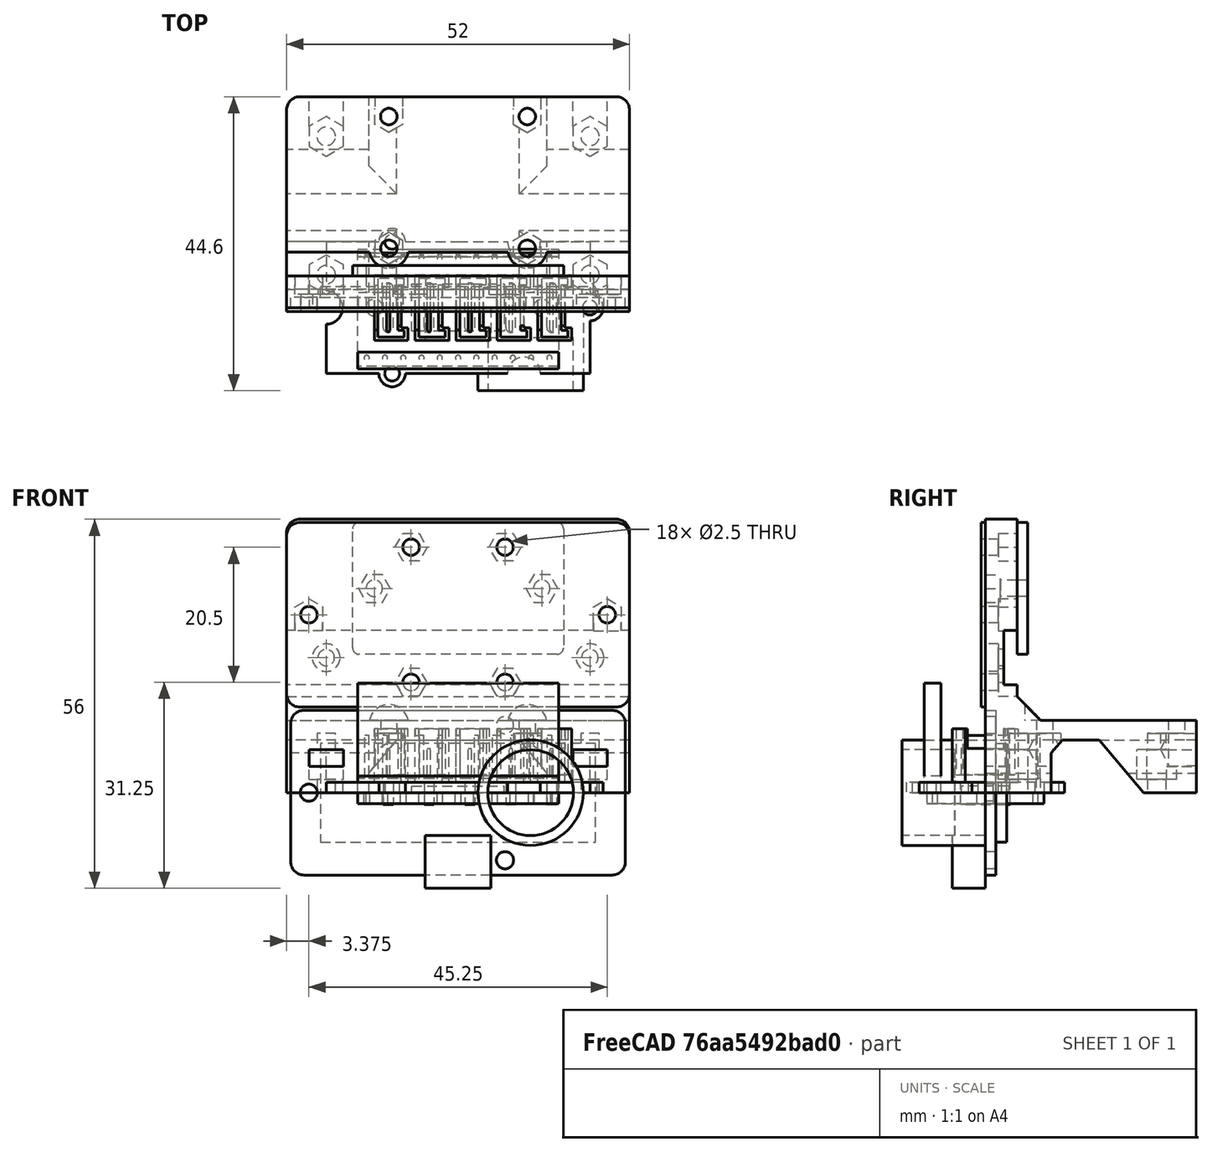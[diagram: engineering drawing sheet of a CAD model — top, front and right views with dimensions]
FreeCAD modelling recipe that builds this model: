
FCSTD DOCUMENT  (FreeCAD 0.19R24276 (Git))
Label: PB3D_TriPlate_USMount
License: All rights reserved
LicenseURL: http://en.wikipedia.org/wiki/All_rights_reserved
objects: Sketcher::SketchObject×54, PartDesign::Pocket×32, PartDesign::Body×30, PartDesign::Pad×20, PartDesign::FeatureBase×14, PartDesign::Plane×8, App::Part×5, PartDesign::LinearPattern×4, Spreadsheet::Sheet×3, Mesh::Feature×2, PartDesign::ShapeBinder×1, PartDesign::Fillet×1
note: 217 computed .brp shape members not serialized (recipe doc carries the construction recipe); baked Part::Feature solids carry a one-line shape summary decoded from their .brp

FEATURE [Spreadsheet::Sheet] Spreadsheet  label="params"
  cells = A1=M2 Bolt Clearances; C1=M2.5 Bolt Clearances; A2=Hole Clear Diam; B2(m2_hole_clear_diam)==2.5mm; C2=Hole Clear Diam; D2(m25_hole_clear_diam)==2.8mm; E2=Std Rad; F2(std_rad)==2mm; A3=Head Clear Diam; B3(m2_head_clear_diam)==4.2mm; C3=Head Clear Diam; D3(m25_head_clear_diam)==5.2mm; E3=Std Rad Min; F3(std_rad_min)==0.6mm; A4=Head Min Depth; B4(m2_head_min_depth)==2mm; C4=Head Min Depth; D4(m25_head_min_depth)==2.3mm; E4=Std Tol Clear; F4(std_tol_clear)==0.3mm; A5=Nut Clear Flat; B5(m2_nut_clear_flat)==4.2mm; C5=Nut Clear Flat; D5(m25_nut_clear_flat)==5.2mm; A6=Nut Min Depth; B6(m2_nut_min_depth)==2mm; C6=Nut Min Depth; D6(m25_nut_min_depth)==2mm; A8=USR Mount; C8=USR Mt To Plate; E8=Grove I2C Hub Mt; G8=Adafruit I2C Exp; A9=USR Mt Width; B9(usr_mt_width)==52mm; C9=MtToPlate Hole Space Offset W; D9(mt_to_plate_hole_space_offset_w)==6mm; E9=I2C Mt Plate Height; F9(i2c_mt_plate_height)==11mm; G9=Exp I2C Mt Height; H9(exp_i2c_mt_height)==31mm; A10=USR Mt Height; B10(usr_mt_height)==41.5mm; C10=MtToPlate Hole Space W; D10(mt_to_plate_hole_space_w)==usr_mt_width - 2 * mt_to_plate_hole_space_offset_w; E10=I2C Mt Plate Thick; F10(i2c_mt_plate_thick)==3mm; G10=Exp I2C Hole Space; H10(exp_i2c_hole_space)==25.4mm; A11=USR Mt Vert Thick; B11(usr_mt_vert_thick_top)==4.8mm; C11=MtToPlate Hole Offset L; D11(mt_to_plate_hole_offset_l)==5mm; E11=I2C Mt Nut Offset; F11(i2c_mt_nut_offset)==2mm; A12=USR Mt Vert Thick Bot; B12(usr_mt_vert_thick_bot)==8.4mm; C12=MtToPlate Hole Loc L; D12(mt_to_plate_hole_loc_l)==26mm; E12=I2C Mt Slot Z; F12(i2c_mt_slot_z)==i2c_mt_plate_height - i2c_mt_nut_offset; A13=USR Mt Foot Width; B13(usr_mt_foot_width)==32mm; E13=I2C Mt Slot Height; F13(i2c_mt_slot_height)==m2_nut_min_depth + 0.5mm; C14=MtToPlate CSunk Z; D14(mt_to_plate_csunk_z)==2mm; E14=I2C Mt CSunk Z; F14(i2c_mt_csunk_z)==i2c_mt_plate_height - i2c_mt_nut_offset; G14=LightSens Mts; A15=USR Mt Hole Width Long; B15(usr_mt_hole_width_long)==22.625mm; C15=MtToPlate CSunk Height; D15(mt_to_plate_csunk_height)==2mm; E15=I2C Mt CSunk Height; F15(i2c_mt_csunk_height)==m2_nut_min_depth; G15=LightSens Loc Z; H15(lightsens_loc_z)==16.5mm; A16=USR Mt Hole Width Short; B16(usr_mt_hole_width_short)==7.125mm; C16=MtToPlate Slot Z; D16(mt_to_plate_slot_z)==mt_to_plate_csunk_z + mt_to_plate_csunk_height; G16=LightMt Height; H16(lightmt_height)==8mm; A17=USR Mt Hole Height; B17(usr_mt_hole_height)==20.5mm; C17=MtToPlate Slot Height; D17(mt_to_plate_slot_height)==m25_nut_min_depth + 0.5mm; E17=I2C Mt Holes Width; F17(i2c_mt_holes_width)==21mm; G17=LightMt Hole Space Leng; H17(lightmt_hole_space_leng)==40mm; A18=USR Mt Hole Cent Loc Z; B18(usr_mt_hole_cent_loc_z)==27mm; E18=I2C Mt Holes Length; F18(i2c_mt_holes_length)==20mm; G18=LightMt Cent Thick; H18(lightmt_thick_cent)==2mm; E19=I2C Mt Holes Offset Leng; F19(i2c_mt_holes_offset_leng)==9mm; A20=USR CSunk Offset; B20(usr_mt_csunk_offset)==2mm; E21=I2C Plate Clear Diam; F21(i2c_plate_clear_diam)==6mm; A22=USR Mt Fr Arch Width; B22(usr_mt_fr_arch_width)==27mm; A23=USR Mt Fr Arch Vert Height; B23(usr_mt_fr_arch_vert_height)==3mm; A24=USR Mt Si Arch Width; B24(usr_mt_side_arch_width)==14mm; A25=USR Mt Si Arch Offset; B25(usr_mt_side_arch_offset)==8mm; A26=USR Mt Si Arch Vert Height; B26(usr_mt_side_arch_vert_height)==6mm
FEATURE [Sketcher::SketchObject] Sketch001
  FullyConstrained = true
  MapMode = 5
  Placement = pos=(0,0,0) rot=(1,0,0;1.5708rad)
  Support = -> [XZ_Plane006]
  sketch-geometry (5):
    g0: Circle CenterX=-22.625 CenterY=0 CenterZ=0 NormalX=0 NormalY=0 NormalZ=1 AngleXU=0 Radius=1.3
    g1: Circle CenterX=7.125 CenterY=10.25 CenterZ=0 NormalX=0 NormalY=0 NormalZ=1 AngleXU=0 Radius=1.3
    g2: Circle CenterX=7.125 CenterY=-10.25 CenterZ=0 NormalX=0 NormalY=0 NormalZ=1 AngleXU=0 Radius=1.3
    g3: LineSegment StartX=7.125 StartY=10.25 StartZ=0 EndX=7.125 EndY=-10.25 EndZ=0
    g4: LineSegment StartX=0 StartY=0 StartZ=0 EndX=7.125 EndY=0 EndZ=0
  constraints (13):
    c: PointOnObject(g0,g-1)
    c: Coincident(g3,g1)
    c: Coincident(g3,g2)
    c: Vertical(g3)
    c: Equal(g0,g1)
    c: Equal(g2,g1)
    c: Diameter(g0) = 2.6
    c: Coincident(g4,g-1)
    c: PointOnObject(g4,g-1)
    c: Symmetric(g1,g2,g4)
    c: Distance(g3) = 20.5
    c: Distance(g4) = 7.125
    c: DistanceX(g0,g-1) = 22.625
FEATURE [PartDesign::ShapeBinder] CopyPocket
  Placement = pos=(0,0,0) rot=(1,0,0;1.5708rad)
  TraceSupport = false
FEATURE [Sketcher::SketchObject] Sketch
  FullyConstrained = true
  MapMode = 5
  Placement = pos=(0,0,0) rot=(1,0,0;1.5708rad)
  Support = -> [XZ_Plane006]
  sketch-geometry (6):
    g0: LineSegment StartX=0 StartY=0 StartZ=0 EndX=0 EndY=12.5 EndZ=0
    g1: LineSegment StartX=0 StartY=0 StartZ=0 EndX=25.375 EndY=0 EndZ=0
    g2: LineSegment StartX=-25.375 StartY=12.5 StartZ=0 EndX=25.375 EndY=12.5 EndZ=0
    g3: LineSegment StartX=25.375 StartY=12.5 StartZ=0 EndX=25.375 EndY=-12.5 EndZ=0
    g4: LineSegment StartX=25.375 StartY=-12.5 StartZ=0 EndX=-25.375 EndY=-12.5 EndZ=0
    g5: LineSegment StartX=-25.375 StartY=-12.5 StartZ=0 EndX=-25.375 EndY=12.5 EndZ=0
  constraints (16):
    c: Coincident(g0,g-1)
    c: PointOnObject(g0,g-2)
    c: Coincident(g1,g-1)
    c: Horizontal(g1)
    c: Coincident(g2,g3)
    c: Coincident(g3,g4)
    c: Coincident(g4,g5)
    c: Coincident(g5,g2)
    c: Horizontal(g2)
    c: Horizontal(g4)
    c: Vertical(g3)
    c: Vertical(g5)
    c: Symmetric(g2,g2,g0)
    c: Symmetric(g2,g3,g1)
    c: Distance(g2) = 50.75
    c: Distance(g3) = 25
FEATURE [PartDesign::Pad] Pad
  Direction = (1,1,1)
  Length = 1.6
  Length2 = 100
  Placement = pos=(0,0,0) rot=(1,0,0;1.5708rad)
  Profile = -> Sketch
  Reversed = true
  Type = 0
FEATURE [PartDesign::Fillet] Fillet
  Base = -> Pad [Edge2,Edge1,Edge8,Edge5]
  BaseFeature = -> Pad
  Placement = pos=(0,0,0) rot=(1,0,0;1.5708rad)
  Radius = 2
  SupportTransform = false
FEATURE [PartDesign::Pocket] Pocket
  BaseFeature = -> Fillet
  Length = 5
  Length2 = 100
  Placement = pos=(0,0,0) rot=(1,0,0;1.5708rad)
  Profile = -> Sketch001
  Type = 1
FEATURE [PartDesign::Body] Body005  label="MainPlate"
  Group = -> [Sketch,Pad,Fillet,Sketch001,Pocket]
  Origin = -> Origin007
  Tip = -> Pocket
FEATURE [Sketcher::SketchObject] Sketch002
  FullyConstrained = true
  MapMode = 5
  Placement = pos=(0,0,0) rot=(1,0,0;1.5708rad)
  Support = -> [XZ_Plane002]
  sketch-geometry (1):
    g0: Circle CenterX=-11 CenterY=0 CenterZ=0 NormalX=0 NormalY=0 NormalZ=1 AngleXU=0 Radius=8
  constraints (3):
    c: PointOnObject(g0,g-1)
    c: DistanceX(g0,g-1) = 11
    c: Diameter(g0) = 16
FEATURE [PartDesign::Pad] Pad001
  Direction = (1,1,1)
  Length = 12.6
  Length2 = 100
  Placement = pos=(0,0,0) rot=(1,0,0;1.5708rad)
  Profile = -> Sketch002
  Type = 0
FEATURE [Sketcher::SketchObject] Sketch004
  FullyConstrained = true
  MapMode = 5
  Placement = pos=(0,0,0) rot=(1,0,0;1.5708rad)
  Support = -> [XZ_Plane004]
  sketch-geometry (5):
    g0: LineSegment StartX=-5 StartY=-6.5 StartZ=0 EndX=5 EndY=-6.5 EndZ=0
    g1: LineSegment StartX=5 StartY=-6.5 StartZ=0 EndX=5 EndY=-14.5 EndZ=0
    g2: LineSegment StartX=5 StartY=-14.5 StartZ=0 EndX=-5 EndY=-14.5 EndZ=0
    g3: LineSegment StartX=-5 StartY=-14.5 StartZ=0 EndX=-5 EndY=-6.5 EndZ=0
    g4: LineSegment StartX=0 StartY=0 StartZ=0 EndX=0 EndY=-6.5 EndZ=0
  constraints (14):
    c: Coincident(g0,g1)
    c: Coincident(g1,g2)
    c: Coincident(g2,g3)
    c: Coincident(g3,g0)
    c: Horizontal(g0)
    c: Horizontal(g2)
    c: Vertical(g1)
    c: Vertical(g3)
    c: Coincident(g4,g-1)
    c: Vertical(g4)
    c: Symmetric(g0,g0,g4)
    c: Distance(g4) = 6.5
    c: Distance(g1) = 8
    c: Distance(g2) = 10
FEATURE [PartDesign::Pad] Pad002
  Direction = (1,1,1)
  Length = 5
  Length2 = 100
  Placement = pos=(0,0,0) rot=(1,0,0;1.5708rad)
  Profile = -> Sketch004
  Type = 0
FEATURE [PartDesign::Body] Body003  label="GroveConnector"
  Group = -> [Sketch004,Pad002]
  Origin = -> Origin004
  Tip = -> Pad002
FEATURE [Sketcher::SketchObject] Sketch003
  FullyConstrained = true
  MapMode = 5
  Placement = pos=(0,-12.6,5.6e-15) rot=(1,0,0;1.5708rad)
  Support = -> [Pad001]
  sketch-geometry (1):
    g0: Circle CenterX=-11 CenterY=0 CenterZ=0 NormalX=0 NormalY=0 NormalZ=1 AngleXU=0 Radius=6.5
  constraints (3):
    c: PointOnObject(g0,g-1)
    c: DistanceX(g0,g-1) = 11
    c: Diameter(g0) = 13
FEATURE [PartDesign::Pocket] Pocket001
  BaseFeature = -> Pad001
  Length = 8
  Length2 = 100
  Placement = pos=(0,0,0) rot=(1,0,0;1.5708rad)
  Profile = -> Sketch003
  Type = 0
FEATURE [PartDesign::Body] Body001  label="USProbeL"
  Group = -> [Sketch002,Pad001,Sketch003,Pocket001]
  Origin = -> Origin006
  Tip = -> Pocket001
FEATURE [Sketcher::SketchObject] Sketch005
  FullyConstrained = true
  MapMode = 5
  Placement = pos=(0,1.6,-7e-16) rot=(-1,0,0;1.5708rad)
  Support = -> [CopyPocket]
  sketch-geometry (6):
    g0: LineSegment StartX=0 StartY=0 StartZ=0 EndX=0 EndY=7.5 EndZ=0
    g1: LineSegment StartX=0 StartY=0 StartZ=0 EndX=20.875 EndY=0 EndZ=0
    g2: LineSegment StartX=-20.875 StartY=7.5 StartZ=0 EndX=20.875 EndY=7.5 EndZ=0
    g3: LineSegment StartX=20.875 StartY=7.5 StartZ=0 EndX=20.875 EndY=-7.5 EndZ=0
    g4: LineSegment StartX=20.875 StartY=-7.5 StartZ=0 EndX=-20.875 EndY=-7.5 EndZ=0
    g5: LineSegment StartX=-20.875 StartY=-7.5 StartZ=0 EndX=-20.875 EndY=7.5 EndZ=0
  constraints (16):
    c: Coincident(g0,g-1)
    c: Vertical(g0)
    c: Coincident(g1,g-1)
    c: Horizontal(g1)
    c: Coincident(g2,g3)
    c: Coincident(g3,g4)
    c: Coincident(g4,g5)
    c: Coincident(g5,g2)
    c: Horizontal(g2)
    c: Horizontal(g4)
    c: Vertical(g3)
    c: Vertical(g5)
    c: Symmetric(g2,g2,g0)
    c: Symmetric(g2,g3,g1)
    c: Distance(g3) = 15
    c: Distance(g2) = 41.75
FEATURE [PartDesign::Pad] Pad003
  Direction = (1,1,1)
  Length = 1.65
  Length2 = 100
  Placement = pos=(0,0,0) rot=(1,0,0;1.5708rad)
  Profile = -> Sketch005
  Type = 0
FEATURE [PartDesign::Body] Body004  label="Chips"
  Group = -> [CopyPocket,Sketch005,Pad003]
  Origin = -> Origin005
  Tip = -> Pad003
FEATURE [PartDesign::FeatureBase] Clone
  BaseFeature = -> Body001
FEATURE [PartDesign::Body] Body002  label="USProbeR"
  BaseFeature = -> Body001
  Group = -> [Clone]
  Origin = -> Origin003
  Placement = pos=(22,0,0) rot=(0,0,1;0rad)
  Tip = -> Clone
FEATURE [App::Part] Part001  label="Grove_USRanger"
  Group = -> [Body005,Body001,Body002,Body003,Body004]
  Origin = -> Origin002
  Placement = pos=(0,-4,27) rot=(0,0,1;0rad)
FEATURE [Sketcher::SketchObject] Sketch012
  FullyConstrained = true
  MapMode = 5
  Support = -> [XY_Plane014]
  sketch-geometry (6):
    g0: Circle CenterX=-10 CenterY=10 CenterZ=0 NormalX=0 NormalY=0 NormalZ=1 AngleXU=0 Radius=1.125
    g1: Circle CenterX=-10 CenterY=-10 CenterZ=0 NormalX=0 NormalY=0 NormalZ=1 AngleXU=0 Radius=1.125
    g2: Circle CenterX=20 CenterY=0 CenterZ=0 NormalX=0 NormalY=0 NormalZ=1 AngleXU=0 Radius=1.125
    g3: LineSegment StartX=-10 StartY=10 StartZ=0 EndX=-10 EndY=-10 EndZ=0
    g4: LineSegment StartX=0 StartY=0 StartZ=0 EndX=20 EndY=0 EndZ=0
    g5: LineSegment StartX=0 StartY=0 StartZ=0 EndX=-10 EndY=0 EndZ=0
  constraints (15):
    c: Coincident(g3,g0)
    c: Coincident(g3,g1)
    c: Coincident(g4,g-1)
    c: Coincident(g4,g2)
    c: Horizontal(g4)
    c: Coincident(g5,g-1)
    c: PointOnObject(g5,g-1)
    c: Symmetric(g0,g1,g5)
    c: Vertical(g3)
    c: Equal(g2,g0)
    c: Equal(g0,g1)
    c: Diameter(g0) = 2.25
    c: Distance(g5) = 10
    c: Distance(g4) = 20
    c: Distance(g3) = 20
FEATURE [Sketcher::SketchObject] Sketch013
  FullyConstrained = true
  MapMode = 5
  Support = -> [XY_Plane014]
  sketch-geometry (26):
    g0: LineSegment StartX=-20 StartY=10 StartZ=0 EndX=-12 EndY=10 EndZ=0
    g1: LineSegment StartX=-8 StartY=10 StartZ=0 EndX=0 EndY=10 EndZ=0
    g2: LineSegment StartX=0 StartY=10 StartZ=0 EndX=7.5 EndY=10 EndZ=0
    g3: LineSegment StartX=12.5 StartY=10 StartZ=0 EndX=20 EndY=10 EndZ=0
    g4: LineSegment StartX=20 StartY=-10 StartZ=0 EndX=12.5 EndY=-10 EndZ=0
    g5: LineSegment StartX=7.5 StartY=-10 StartZ=0 EndX=0 EndY=-10 EndZ=0
    g6: LineSegment StartX=0 StartY=-10 StartZ=0 EndX=-8 EndY=-10 EndZ=0
    g7: LineSegment StartX=-12 StartY=-10 StartZ=0 EndX=-20 EndY=-10 EndZ=0
    g8: LineSegment StartX=-12 StartY=10 StartZ=0 EndX=-8 EndY=10 EndZ=0
    g9: LineSegment StartX=-12 StartY=-10 StartZ=0 EndX=-8 EndY=-10 EndZ=0
    g10: LineSegment StartX=7.5 StartY=10 StartZ=0 EndX=12.5 EndY=10 EndZ=0
    g11: LineSegment StartX=7.5 StartY=-10 StartZ=0 EndX=12.5 EndY=-10 EndZ=0
    g12: LineSegment StartX=20 StartY=10 StartZ=0 EndX=20 EndY=2 EndZ=0
    g13: LineSegment StartX=20 StartY=-10 StartZ=0 EndX=20 EndY=-2 EndZ=0
    g14: LineSegment StartX=-20 StartY=-2.5 StartZ=0 EndX=-20 EndY=2.5 EndZ=0
    g15: LineSegment StartX=20 StartY=2 StartZ=0 EndX=20 EndY=-2 EndZ=0
    g16: ArcOfCircle CenterX=20 CenterY=0 CenterZ=0 NormalX=0 NormalY=0 NormalZ=1 AngleXU=0 Radius=2 StartAngle=4.71239 EndAngle=7.85398
    g17: ArcOfCircle CenterX=-10 CenterY=10 CenterZ=0 NormalX=0 NormalY=0 NormalZ=1 AngleXU=0 Radius=2 StartAngle=-9e-16 EndAngle=3.14159
    g18: ArcOfCircle CenterX=-10 CenterY=-10 CenterZ=0 NormalX=0 NormalY=0 NormalZ=1 AngleXU=0 Radius=2 StartAngle=3.14159 EndAngle=6.28319
    g19: ArcOfCircle CenterX=10 CenterY=10 CenterZ=0 NormalX=0 NormalY=0 NormalZ=1 AngleXU=0 Radius=2.5 StartAngle=3.14159 EndAngle=6.28319
    g20: ArcOfCircle CenterX=10 CenterY=-10 CenterZ=0 NormalX=0 NormalY=0 NormalZ=1 AngleXU=0 Radius=2.5 StartAngle=1e-15 EndAngle=3.14159
    g21: LineSegment StartX=-10 StartY=10 StartZ=0 EndX=-10 EndY=-10 EndZ=0
    g22: LineSegment StartX=10 StartY=10 StartZ=0 EndX=10 EndY=-10 EndZ=0
    g23: LineSegment StartX=-20 StartY=10 StartZ=0 EndX=-20 EndY=2.5 EndZ=0
    g24: LineSegment StartX=-20 StartY=-10 StartZ=0 EndX=-20 EndY=-2.5 EndZ=0
    g25: ArcOfCircle CenterX=-20 CenterY=0 CenterZ=0 NormalX=0 NormalY=0 NormalZ=1 AngleXU=0 Radius=2.5 StartAngle=4.71239 EndAngle=7.85398
  constraints (76):
    c: Horizontal(g0)
    c: PointOnObject(g1,g-2)
    c: Horizontal(g1)
    c: Coincident(g2,g1)
    c: Horizontal(g2)
    c: Horizontal(g3)
    c: Horizontal(g4)
    c: PointOnObject(g5,g-2)
    c: Horizontal(g5)
    c: Coincident(g6,g5)
    c: Horizontal(g6)
    c: Horizontal(g7)
    c: Coincident(g8,g0)
    c: Coincident(g8,g1)
    c: Horizontal(g8)
    c: Coincident(g9,g7)
    c: Coincident(g9,g6)
    c: Coincident(g10,g2)
    c: Coincident(g10,g3)
    c: Horizontal(g10)
    c: Coincident(g11,g5)
    c: Coincident(g11,g4)
    c: Horizontal(g11)
    c: Horizontal(g9)
    c: Coincident(g12,g3)
    c: Coincident(g13,g4)
    c: Vertical(g13)
    c: Vertical(g14)
    c: Coincident(g15,g12)
    c: Coincident(g15,g13)
    c: Vertical(g15)
    c: Vertical(g12)
    c: PointOnObject(g16,g-1)
    c: Coincident(g16,g12)
    c: Coincident(g16,g13)
    c: PointOnObject(g16,g15)
    c: Coincident(g17,g0)
    c: Coincident(g17,g1)
    c: Coincident(g18,g7)
    c: Coincident(g18,g6)
    c: Coincident(g19,g2)
    c: Coincident(g19,g3)
    c: Coincident(g20,g5)
    c: Coincident(g20,g4)
    c: Coincident(g21,g17)
    c: Coincident(g21,g18)
    c: Vertical(g21)
    c: Coincident(g22,g19)
    c: Coincident(g22,g20)
    c: Vertical(g22)
    c: Equal(g17,g18)
    c: Equal(g18,g16)
    c: Equal(g20,g19)
    c: PointOnObject(g19,g10)
    c: PointOnObject(g20,g11)
    c: PointOnObject(g17,g8)
    c: PointOnObject(g18,g9)
    c: Diameter(g17) = 4
    c: Equal(g1,g0)
    c: Equal(g2,g3)
    c: DistanceX(g0,g3) = 40
    c: DistanceX(g1,g3) = 20
    c: DistanceY(g4,g3) = 20
    c: Coincident(g23,g0)
    c: Vertical(g23)
    c: Coincident(g24,g7)
    c: Vertical(g24)
    c: Equal(g23,g24)
    c: PointOnObject(g25,g-1)
    c: Coincident(g25,g23)
    c: Coincident(g25,g24)
    c: Diameter(g19) = 5
    c: Equal(g25,g19)
    c: PointOnObject(g25,g14)
    c: Coincident(g14,g23)
    c: Coincident(g14,g24)
FEATURE [PartDesign::Pad] Pad008
  Direction = (1,1,1)
  Length = 1.6
  Length2 = 100
  Profile = -> Sketch013
  Type = 0
FEATURE [PartDesign::Pocket] Pocket004
  BaseFeature = -> Pad008
  Length = 5
  Length2 = 100
  Profile = -> Sketch012
  Reversed = true
  Type = 1
FEATURE [PartDesign::Body] Body006  label="GroveDBoard"
  Group = -> [Sketch013,Pad008,Sketch012,Pocket004]
  Origin = -> Origin008
  Tip = -> Pocket004
FEATURE [Sketcher::SketchObject] Sketch008
  FullyConstrained = true
  MapMode = 5
  Support = -> [XY_Plane015]
  sketch-geometry (8):
    g0: LineSegment StartX=-5 StartY=0 StartZ=0 EndX=-3.05 EndY=0 EndZ=0
    g1: LineSegment StartX=3.05 StartY=0 StartZ=0 EndX=5 EndY=0 EndZ=0
    g2: LineSegment StartX=-5 StartY=0 StartZ=0 EndX=-5 EndY=5.1 EndZ=0
    g3: LineSegment StartX=-5 StartY=5.1 StartZ=0 EndX=5 EndY=5.1 EndZ=0
    g4: LineSegment StartX=5 StartY=5.1 StartZ=0 EndX=5 EndY=0 EndZ=0
    g5: LineSegment StartX=3.05 StartY=0 StartZ=0 EndX=3.05 EndY=1 EndZ=0
    g6: LineSegment StartX=3.05 StartY=1 StartZ=0 EndX=-3.05 EndY=1 EndZ=0
    g7: LineSegment StartX=-3.05 StartY=1 StartZ=0 EndX=-3.05 EndY=0 EndZ=0
  constraints (23):
    c: PointOnObject(g0,g-1)
    c: PointOnObject(g1,g-1)
    c: PointOnObject(g0,g-1)
    c: Coincident(g2,g0)
    c: Vertical(g2)
    c: Coincident(g3,g2)
    c: Horizontal(g3)
    c: Coincident(g4,g3)
    c: Coincident(g4,g1)
    c: Vertical(g4)
    c: Coincident(g5,g1)
    c: Vertical(g5)
    c: Coincident(g6,g5)
    c: Horizontal(g6)
    c: Coincident(g7,g6)
    c: Coincident(g7,g0)
    c: Vertical(g7)
    c: Equal(g0,g1)
    c: Symmetric(g0,g1,g-1)
    c: Distance(g4) = 5.1
    c: Distance(g6) = 6.1
    c: Distance(g3) = 10
    c: Distance(g7) = 1
FEATURE [PartDesign::Pad] Pad005
  Direction = (1,1,1)
  Length = 8.1
  Length2 = 100
  Profile = -> Sketch008
  Type = 0
FEATURE [Sketcher::SketchObject] Sketch009
  FullyConstrained = true
  MapMode = 5
  Placement = pos=(0,0,8.1) rot=(0,0,1;0rad)
  Support = -> [Pad005]
  sketch-geometry (10):
    g0: LineSegment StartX=-4.45 StartY=0.55 StartZ=0 EndX=-3.45 EndY=0.55 EndZ=0
    g1: LineSegment StartX=-3.45 StartY=0.55 StartZ=0 EndX=-3.45 EndY=1.55 EndZ=0
    g2: LineSegment StartX=-3.45 StartY=1.55 StartZ=0 EndX=3.45 EndY=1.55 EndZ=0
    g3: LineSegment StartX=3.45 StartY=1.55 StartZ=0 EndX=3.45 EndY=0.55 EndZ=0
    g4: LineSegment StartX=3.45 StartY=0.55 StartZ=0 EndX=4.45 EndY=0.55 EndZ=0
    g5: LineSegment StartX=4.45 StartY=0.55 StartZ=0 EndX=4.45 EndY=4.55 EndZ=0
    g6: LineSegment StartX=4.45 StartY=4.55 StartZ=0 EndX=-4.45 EndY=4.55 EndZ=0
    g7: LineSegment StartX=-4.45 StartY=4.55 StartZ=0 EndX=-4.45 EndY=0.55 EndZ=0
    g8: LineSegment StartX=-3.45 StartY=0.55 StartZ=0 EndX=3.45 EndY=0.55 EndZ=0
    g9: LineSegment StartX=0 StartY=0 StartZ=0 EndX=0 EndY=0.55 EndZ=0
  constraints (28):
    c: Horizontal(g0)
    c: Coincident(g1,g0)
    c: Coincident(g2,g1)
    c: Horizontal(g2)
    c: Coincident(g3,g2)
    c: Vertical(g3)
    c: Coincident(g4,g3)
    c: Horizontal(g4)
    c: Coincident(g5,g4)
    c: Vertical(g5)
    c: Coincident(g6,g5)
    c: Horizontal(g6)
    c: Coincident(g7,g6)
    c: Coincident(g7,g0)
    c: Vertical(g7)
    c: Vertical(g1)
    c: Coincident(g8,g0)
    c: Coincident(g8,g3)
    c: Horizontal(g8)
    c: Equal(g0,g4)
    c: Coincident(g9,g-1)
    c: PointOnObject(g9,g-2)
    c: Symmetric(g0,g3,g9)
    c: Distance(g0) = 1
    c: Distance(g1) = 1
    c: Distance(g9) = 0.55
    c: Distance(g6) = 8.9
    c: DistanceY(g2,g5) = 3
FEATURE [PartDesign::Pocket] Pocket003
  BaseFeature = -> Pad005
  Length = 7
  Length2 = 100
  Profile = -> Sketch009
  Type = 0
FEATURE [Sketcher::SketchObject] Sketch014
  FullyConstrained = true
  MapMode = 5
  Support = -> [XY_Plane015]
  sketch-geometry (5):
    g0: ArcOfCircle CenterX=-3 CenterY=3 CenterZ=0 NormalX=0 NormalY=0 NormalZ=1 AngleXU=0 Radius=0.75 StartAngle=1.5708 EndAngle=4.71239
    g1: ArcOfCircle CenterX=3 CenterY=3 CenterZ=0 NormalX=0 NormalY=0 NormalZ=1 AngleXU=0 Radius=0.75 StartAngle=4.71239 EndAngle=7.85398
    g2: LineSegment StartX=-3 StartY=2.25 StartZ=0 EndX=3 EndY=2.25 EndZ=0
    g3: LineSegment StartX=-3 StartY=3.75 StartZ=0 EndX=3 EndY=3.75 EndZ=0
    g4: LineSegment StartX=0 StartY=0 StartZ=0 EndX=0 EndY=3 EndZ=0
  constraints (12):
    c: Tangent(g0,g3) = 1.5708
    c: Tangent(g0,g2) = -1.5708
    c: Tangent(g2,g1) = -1.5708
    c: Tangent(g3,g1) = 1.5708
    c: Horizontal(g2)
    c: Equal(g0,g1)
    c: Coincident(g4,g-1)
    c: PointOnObject(g4,g-2)
    c: Symmetric(g0,g1,g4)
    c: Distance(g4) = 3
    c: DistanceY(g1,g1) = 1.5
    c: DistanceX(g0,g1) = 6
FEATURE [Sketcher::SketchObject] Sketch010
  FullyConstrained = true
  MapMode = 5
  Placement = pos=(0,0,8.1) rot=(0,0,1;0rad)
  Support = -> [Pocket003]
  sketch-geometry (5):
    g0: LineSegment StartX=0 StartY=0 StartZ=0 EndX=0 EndY=3 EndZ=0
    g1: LineSegment StartX=-3.4 StartY=8 StartZ=0 EndX=3.4 EndY=8 EndZ=0
    g2: LineSegment StartX=3.4 StartY=8 StartZ=0 EndX=3.4 EndY=3 EndZ=0
    g3: LineSegment StartX=3.4 StartY=3 StartZ=0 EndX=-3.4 EndY=3 EndZ=0
    g4: LineSegment StartX=-3.4 StartY=3 StartZ=0 EndX=-3.4 EndY=8 EndZ=0
  constraints (14):
    c: Coincident(g0,g-1)
    c: PointOnObject(g0,g-2)
    c: Coincident(g1,g2)
    c: Coincident(g2,g3)
    c: Coincident(g3,g4)
    c: Coincident(g4,g1)
    c: Horizontal(g1)
    c: Horizontal(g3)
    c: Vertical(g2)
    c: Vertical(g4)
    c: Symmetric(g3,g2,g0)
    c: Distance(g0) = 3
    c: Distance(g2) = 5
    c: Distance(g1) = 6.8
FEATURE [PartDesign::Pocket] Pocket006
  BaseFeature = -> Pocket003
  Length = 1
  Length2 = 100
  Profile = -> Sketch010
  Type = 0
FEATURE [Sketcher::SketchObject] Sketch011
  FullyConstrained = true
  MapMode = 5
  Placement = pos=(0,0,8.1) rot=(0,0,1;0rad)
  Support = -> [Pocket006]
  sketch-geometry (4):
    g0: LineSegment StartX=-2.75 StartY=3 StartZ=0 EndX=2.75 EndY=3 EndZ=0
    g1: LineSegment StartX=2.75 StartY=3 StartZ=0 EndX=2.75 EndY=0 EndZ=0
    g2: LineSegment StartX=2.75 StartY=0 StartZ=0 EndX=-2.75 EndY=0 EndZ=0
    g3: LineSegment StartX=-2.75 StartY=0 StartZ=0 EndX=-2.75 EndY=3 EndZ=0
  constraints (11):
    c: Coincident(g0,g1)
    c: Coincident(g1,g2)
    c: Coincident(g2,g3)
    c: Coincident(g3,g0)
    c: Horizontal(g0)
    c: Horizontal(g2)
    c: Vertical(g1)
    c: Vertical(g3)
    c: Symmetric(g2,g1,g-1)
    c: Distance(g1) = 3
    c: Distance(g0) = 5.5
FEATURE [PartDesign::Pocket] Pocket005
  BaseFeature = -> Pocket006
  Length = 3
  Length2 = 100
  Profile = -> Sketch011
  Type = 0
FEATURE [Sketcher::SketchObject] Sketch015
  FullyConstrained = true
  MapMode = 5
  Placement = pos=(0,0,1.1) rot=(0,0,1;0rad)
  Support = -> [Pocket005]
  sketch-geometry (5):
    g0: ArcOfCircle CenterX=-3.4 CenterY=3 CenterZ=0 NormalX=0 NormalY=0 NormalZ=1 AngleXU=0 Radius=0.25 StartAngle=1.5708 EndAngle=4.71239
    g1: ArcOfCircle CenterX=3.4 CenterY=3 CenterZ=0 NormalX=0 NormalY=0 NormalZ=1 AngleXU=0 Radius=0.25 StartAngle=4.71239 EndAngle=7.85398
    g2: LineSegment StartX=-3.4 StartY=2.75 StartZ=0 EndX=3.4 EndY=2.75 EndZ=0
    g3: LineSegment StartX=-3.4 StartY=3.25 StartZ=0 EndX=3.4 EndY=3.25 EndZ=0
    g4: LineSegment StartX=0 StartY=0 StartZ=0 EndX=0 EndY=2.75 EndZ=0
  constraints (12):
    c: Tangent(g0,g3) = 1.5708
    c: Tangent(g0,g2) = -1.5708
    c: Tangent(g2,g1) = -1.5708
    c: Tangent(g3,g1) = 1.5708
    c: Horizontal(g2)
    c: Equal(g0,g1)
    c: Coincident(g4,g-1)
    c: PointOnObject(g4,g-2)
    c: Symmetric(g0,g1,g4)
    c: DistanceY(g-1,g1) = 3
    c: DistanceY(g1,g1) = 0.5
    c: DistanceX(g0,g1) = 6.8
FEATURE [PartDesign::Pad] Pad006
  BaseFeature = -> Pocket005
  Direction = (1,1,1)
  Length = 4
  Length2 = 100
  Profile = -> Sketch015
  Type = 0
FEATURE [PartDesign::Pad] Pad007
  BaseFeature = -> Pad006
  Direction = (1,1,1)
  Length = 3.4
  Length2 = 100
  Profile = -> Sketch014
  Reversed = true
  Type = 0
FEATURE [PartDesign::Body] Body007  label="GroveHeader1"
  Group = -> [Sketch008,Pad005,Sketch009,Pocket003,Sketch010,Pocket006,Sketch011,Pocket005,Sketch015,Pad006,Sketch014,Pad007]
  Origin = -> Origin015
  Placement = pos=(-13.8,0,1.6) rot=(0,0,1;1.5708rad)
  Tip = -> Pad007
FEATURE [PartDesign::FeatureBase] Clone003
  BaseFeature = -> Body007
  Placement = pos=(-14,0,1.6) rot=(0,0,1;1.5708rad)
FEATURE [PartDesign::Body] Body009  label="GroveHeader5"
  BaseFeature = -> Body007
  Group = -> [Clone003]
  Origin = -> Origin013
  Placement = pos=(25,0,0) rot=(0,0,1;0rad)
  Tip = -> Clone003
FEATURE [PartDesign::FeatureBase] Clone002
  BaseFeature = -> Body007
  Placement = pos=(-14,0,1.6) rot=(0,0,1;1.5708rad)
FEATURE [PartDesign::Body] Body010  label="GroveHeader4"
  BaseFeature = -> Body007
  Group = -> [Clone002]
  Origin = -> Origin011
  Placement = pos=(18.8,0,0) rot=(0,0,1;0rad)
  Tip = -> Clone002
FEATURE [PartDesign::FeatureBase] Clone001
  BaseFeature = -> Body007
  Placement = pos=(-14,0,1.6) rot=(0,0,1;1.5708rad)
FEATURE [PartDesign::Body] Body008  label="GroveHeader3"
  BaseFeature = -> Body007
  Group = -> [Clone001]
  Origin = -> Origin010
  Placement = pos=(12.6,0,0) rot=(0,0,1;0rad)
  Tip = -> Clone001
FEATURE [PartDesign::FeatureBase] Clone004
  BaseFeature = -> Body007
  Placement = pos=(-14,0,1.6) rot=(0,0,1;1.5708rad)
FEATURE [PartDesign::Body] Body011  label="GroveHeader6"
  BaseFeature = -> Body007
  Group = -> [Clone004]
  Origin = -> Origin014
  Placement = pos=(31.2,0,0) rot=(0,0,1;0rad)
  Tip = -> Clone004
FEATURE [PartDesign::FeatureBase] Clone005
  BaseFeature = -> Body007
  Placement = pos=(-14,0,1.6) rot=(0,0,1;1.5708rad)
FEATURE [PartDesign::Body] Body012  label="GroveHeader2"
  BaseFeature = -> Body007
  Group = -> [Clone005]
  Origin = -> Origin012
  Placement = pos=(6.4,0,0) rot=(0,0,1;0rad)
  Tip = -> Clone005
FEATURE [App::Part] Part002  label="Grove_I2CHub6_Part1"
  Group = -> [Body006,Body007,Body012,Body008,Body010,Body009,Body011]
  Origin = -> Origin009
  Placement = pos=(-20.5,19,11) rot=(0,0,1;3.14159rad)
FEATURE [Sketcher::SketchObject] Sketch016
  FullyConstrained = true
  MapMode = 5
  Placement = pos=(0,0,0) rot=(0.57735,0.57735,0.57735;2.0944rad)
  Support = -> [YZ_Plane001]
  expr: Constraints[7] = Spreadsheet.usr_mt_height
  expr: Constraints[13] = <<params>>.usr_mt_vert_thick_bot
  expr: Constraints[8] = <<params>>.usr_mt_vert_thick_top
  expr: Constraints[9] = <<params>>.i2c_mt_plate_height
  expr: Constraints[14] = <<params>>.usr_mt_foot_width
  sketch-geometry (8):
    g0: LineSegment StartX=0 StartY=0 StartZ=0 EndX=32 EndY=0 EndZ=0
    g1: LineSegment StartX=0 StartY=0 StartZ=0 EndX=0 EndY=41.5 EndZ=0
    g2: LineSegment StartX=0 StartY=41.5 StartZ=0 EndX=4.8 EndY=41.5 EndZ=0
    g3: LineSegment StartX=8.4 StartY=11 StartZ=0 EndX=32 EndY=11 EndZ=0
    g4: LineSegment StartX=32 StartY=0 StartZ=0 EndX=32 EndY=11 EndZ=0
    g5: LineSegment StartX=4.8 StartY=41.5 StartZ=0 EndX=4.8 EndY=14.6 EndZ=0
    g6: LineSegment StartX=8.4 StartY=11 StartZ=0 EndX=4.8 EndY=14.6 EndZ=0
    g7: LineSegment StartX=8.4 StartY=11 StartZ=0 EndX=0 EndY=11 EndZ=0
  constraints (23):
    c: Coincident(g0,g-1)
    c: PointOnObject(g0,g-1)
    c: Coincident(g1,g0)
    c: PointOnObject(g1,g-2)
    c: Coincident(g2,g1)
    c: Horizontal(g2)
    c: Horizontal(g3)
    c: DistanceY(g0,g1) = 41.5
    c: DistanceX(g1,g2) = 4.8
    c: DistanceY(g0,g3) = 11
    c: Coincident(g4,g0)
    c: Vertical(g4)
    c: Coincident(g3,g4)
    c: DistanceX(g0,g3) = 8.4
    c: DistanceX(g0,g0) = 32
    c: Coincident(g5,g2)
    c: Vertical(g5)
    c: Coincident(g6,g3)
    c: Coincident(g6,g5)
    c: Coincident(g7,g3)
    c: PointOnObject(g7,g1)
    c: Horizontal(g7)
    c: Angle(g6,g7) = 0.785398
FEATURE [PartDesign::Pad] Pad009  label="MainSideExt"
  Direction = (1,1,1)
  Length = 52
  Length2 = 100
  Midplane = true
  Placement = pos=(0,0,0) rot=(0.57735,0.57735,0.57735;2.0944rad)
  Profile = -> Sketch016
  Type = 0
  expr: Length = Spreadsheet.usr_mt_width
FEATURE [Sketcher::SketchObject] Sketch017
  FullyConstrained = true
  MapMode = 5
  Support = -> [XY_Plane022]
  sketch-geometry (6):
    g0: Circle CenterX=-10 CenterY=10 CenterZ=0 NormalX=0 NormalY=0 NormalZ=1 AngleXU=0 Radius=1.125
    g1: Circle CenterX=-10 CenterY=-10 CenterZ=0 NormalX=0 NormalY=0 NormalZ=1 AngleXU=0 Radius=1.125
    g2: Circle CenterX=20 CenterY=0 CenterZ=0 NormalX=0 NormalY=0 NormalZ=1 AngleXU=0 Radius=1.125
    g3: LineSegment StartX=-10 StartY=10 StartZ=0 EndX=-10 EndY=-10 EndZ=0
    g4: LineSegment StartX=0 StartY=0 StartZ=0 EndX=20 EndY=0 EndZ=0
    g5: LineSegment StartX=0 StartY=0 StartZ=0 EndX=-10 EndY=0 EndZ=0
  constraints (15):
    c: Coincident(g3,g0)
    c: Coincident(g3,g1)
    c: Coincident(g4,g-1)
    c: Coincident(g4,g2)
    c: Horizontal(g4)
    c: Coincident(g5,g-1)
    c: PointOnObject(g5,g-1)
    c: Symmetric(g0,g1,g5)
    c: Vertical(g3)
    c: Equal(g2,g0)
    c: Equal(g0,g1)
    c: Diameter(g0) = 2.25
    c: Distance(g5) = 10
    c: Distance(g4) = 20
    c: Distance(g3) = 20
FEATURE [Sketcher::SketchObject] Sketch019
  FullyConstrained = true
  MapMode = 5
  Support = -> [XY_Plane021]
  sketch-geometry (5):
    g0: ArcOfCircle CenterX=-3 CenterY=3 CenterZ=0 NormalX=0 NormalY=0 NormalZ=1 AngleXU=0 Radius=0.75 StartAngle=1.5708 EndAngle=4.71239
    g1: ArcOfCircle CenterX=3 CenterY=3 CenterZ=0 NormalX=0 NormalY=0 NormalZ=1 AngleXU=0 Radius=0.75 StartAngle=4.71239 EndAngle=7.85398
    g2: LineSegment StartX=-3 StartY=2.25 StartZ=0 EndX=3 EndY=2.25 EndZ=0
    g3: LineSegment StartX=-3 StartY=3.75 StartZ=0 EndX=3 EndY=3.75 EndZ=0
    g4: LineSegment StartX=0 StartY=0 StartZ=0 EndX=0 EndY=3 EndZ=0
  constraints (12):
    c: Tangent(g0,g3) = 1.5708
    c: Tangent(g0,g2) = -1.5708
    c: Tangent(g2,g1) = -1.5708
    c: Tangent(g3,g1) = 1.5708
    c: Horizontal(g2)
    c: Equal(g0,g1)
    c: Coincident(g4,g-1)
    c: PointOnObject(g4,g-2)
    c: Symmetric(g0,g1,g4)
    c: Distance(g4) = 3
    c: DistanceY(g1,g1) = 1.5
    c: DistanceX(g0,g1) = 6
FEATURE [Sketcher::SketchObject] Sketch020
  FullyConstrained = true
  MapMode = 5
  Support = -> [XY_Plane022]
  sketch-geometry (26):
    g0: LineSegment StartX=-20 StartY=10 StartZ=0 EndX=-12 EndY=10 EndZ=0
    g1: LineSegment StartX=-8 StartY=10 StartZ=0 EndX=0 EndY=10 EndZ=0
    g2: LineSegment StartX=0 StartY=10 StartZ=0 EndX=7.5 EndY=10 EndZ=0
    g3: LineSegment StartX=12.5 StartY=10 StartZ=0 EndX=20 EndY=10 EndZ=0
    g4: LineSegment StartX=20 StartY=-10 StartZ=0 EndX=12.5 EndY=-10 EndZ=0
    g5: LineSegment StartX=7.5 StartY=-10 StartZ=0 EndX=0 EndY=-10 EndZ=0
    g6: LineSegment StartX=0 StartY=-10 StartZ=0 EndX=-8 EndY=-10 EndZ=0
    g7: LineSegment StartX=-12 StartY=-10 StartZ=0 EndX=-20 EndY=-10 EndZ=0
    g8: LineSegment StartX=-12 StartY=10 StartZ=0 EndX=-8 EndY=10 EndZ=0
    g9: LineSegment StartX=-12 StartY=-10 StartZ=0 EndX=-8 EndY=-10 EndZ=0
    g10: LineSegment StartX=7.5 StartY=10 StartZ=0 EndX=12.5 EndY=10 EndZ=0
    g11: LineSegment StartX=7.5 StartY=-10 StartZ=0 EndX=12.5 EndY=-10 EndZ=0
    g12: LineSegment StartX=20 StartY=10 StartZ=0 EndX=20 EndY=2 EndZ=0
    g13: LineSegment StartX=20 StartY=-10 StartZ=0 EndX=20 EndY=-2 EndZ=0
    g14: LineSegment StartX=-20 StartY=-2.5 StartZ=0 EndX=-20 EndY=2.5 EndZ=0
    g15: LineSegment StartX=20 StartY=2 StartZ=0 EndX=20 EndY=-2 EndZ=0
    g16: ArcOfCircle CenterX=20 CenterY=0 CenterZ=0 NormalX=0 NormalY=0 NormalZ=1 AngleXU=0 Radius=2 StartAngle=4.71239 EndAngle=7.85398
    g17: ArcOfCircle CenterX=-10 CenterY=10 CenterZ=0 NormalX=0 NormalY=0 NormalZ=1 AngleXU=0 Radius=2 StartAngle=-9e-16 EndAngle=3.14159
    g18: ArcOfCircle CenterX=-10 CenterY=-10 CenterZ=0 NormalX=0 NormalY=0 NormalZ=1 AngleXU=0 Radius=2 StartAngle=3.14159 EndAngle=6.28319
    g19: ArcOfCircle CenterX=10 CenterY=10 CenterZ=0 NormalX=0 NormalY=0 NormalZ=1 AngleXU=0 Radius=2.5 StartAngle=3.14159 EndAngle=6.28319
    g20: ArcOfCircle CenterX=10 CenterY=-10 CenterZ=0 NormalX=0 NormalY=0 NormalZ=1 AngleXU=0 Radius=2.5 StartAngle=1e-15 EndAngle=3.14159
    g21: LineSegment StartX=-10 StartY=10 StartZ=0 EndX=-10 EndY=-10 EndZ=0
    g22: LineSegment StartX=10 StartY=10 StartZ=0 EndX=10 EndY=-10 EndZ=0
    g23: LineSegment StartX=-20 StartY=10 StartZ=0 EndX=-20 EndY=2.5 EndZ=0
    g24: LineSegment StartX=-20 StartY=-10 StartZ=0 EndX=-20 EndY=-2.5 EndZ=0
    g25: ArcOfCircle CenterX=-20 CenterY=0 CenterZ=0 NormalX=0 NormalY=0 NormalZ=1 AngleXU=0 Radius=2.5 StartAngle=4.71239 EndAngle=7.85398
  constraints (76):
    c: Horizontal(g0)
    c: PointOnObject(g1,g-2)
    c: Horizontal(g1)
    c: Coincident(g2,g1)
    c: Horizontal(g2)
    c: Horizontal(g3)
    c: Horizontal(g4)
    c: PointOnObject(g5,g-2)
    c: Horizontal(g5)
    c: Coincident(g6,g5)
    c: Horizontal(g6)
    c: Horizontal(g7)
    c: Coincident(g8,g0)
    c: Coincident(g8,g1)
    c: Horizontal(g8)
    c: Coincident(g9,g7)
    c: Coincident(g9,g6)
    c: Coincident(g10,g2)
    c: Coincident(g10,g3)
    c: Horizontal(g10)
    c: Coincident(g11,g5)
    c: Coincident(g11,g4)
    c: Horizontal(g11)
    c: Horizontal(g9)
    c: Coincident(g12,g3)
    c: Coincident(g13,g4)
    c: Vertical(g13)
    c: Vertical(g14)
    c: Coincident(g15,g12)
    c: Coincident(g15,g13)
    c: Vertical(g15)
    c: Vertical(g12)
    c: PointOnObject(g16,g-1)
    c: Coincident(g16,g12)
    c: Coincident(g16,g13)
    c: PointOnObject(g16,g15)
    c: Coincident(g17,g0)
    c: Coincident(g17,g1)
    c: Coincident(g18,g7)
    c: Coincident(g18,g6)
    c: Coincident(g19,g2)
    c: Coincident(g19,g3)
    c: Coincident(g20,g5)
    c: Coincident(g20,g4)
    c: Coincident(g21,g17)
    c: Coincident(g21,g18)
    c: Vertical(g21)
    c: Coincident(g22,g19)
    c: Coincident(g22,g20)
    c: Vertical(g22)
    c: Equal(g17,g18)
    c: Equal(g18,g16)
    c: Equal(g20,g19)
    c: PointOnObject(g19,g10)
    c: PointOnObject(g20,g11)
    c: PointOnObject(g17,g8)
    c: PointOnObject(g18,g9)
    c: Diameter(g17) = 4
    c: Equal(g1,g0)
    c: Equal(g2,g3)
    c: DistanceX(g0,g3) = 40
    c: DistanceX(g1,g3) = 20
    c: DistanceY(g4,g3) = 20
    c: Coincident(g23,g0)
    c: Vertical(g23)
    c: Coincident(g24,g7)
    c: Vertical(g24)
    c: Equal(g23,g24)
    c: PointOnObject(g25,g-1)
    c: Coincident(g25,g23)
    c: Coincident(g25,g24)
    c: Diameter(g19) = 5
    c: Equal(g25,g19)
    c: PointOnObject(g25,g14)
    c: Coincident(g14,g23)
    c: Coincident(g14,g24)
FEATURE [PartDesign::Pad] Pad012
  Direction = (1,1,1)
  Length = 1.6
  Length2 = 100
  Profile = -> Sketch020
  Type = 0
FEATURE [PartDesign::Pocket] Pocket008
  BaseFeature = -> Pad012
  Length = 5
  Length2 = 100
  Profile = -> Sketch017
  Reversed = true
  Type = 1
FEATURE [PartDesign::Body] Body013  label="GroveDBoard001"
  Group = -> [Sketch020,Pad012,Sketch017,Pocket008]
  Origin = -> Origin021
  Tip = -> Pocket008
FEATURE [Sketcher::SketchObject] Sketch022
  FullyConstrained = true
  MapMode = 5
  Support = -> [XY_Plane021]
  sketch-geometry (8):
    g0: LineSegment StartX=-5 StartY=0 StartZ=0 EndX=-3.05 EndY=0 EndZ=0
    g1: LineSegment StartX=3.05 StartY=0 StartZ=0 EndX=5 EndY=0 EndZ=0
    g2: LineSegment StartX=-5 StartY=0 StartZ=0 EndX=-5 EndY=5.1 EndZ=0
    g3: LineSegment StartX=-5 StartY=5.1 StartZ=0 EndX=5 EndY=5.1 EndZ=0
    g4: LineSegment StartX=5 StartY=5.1 StartZ=0 EndX=5 EndY=0 EndZ=0
    g5: LineSegment StartX=3.05 StartY=0 StartZ=0 EndX=3.05 EndY=1 EndZ=0
    g6: LineSegment StartX=3.05 StartY=1 StartZ=0 EndX=-3.05 EndY=1 EndZ=0
    g7: LineSegment StartX=-3.05 StartY=1 StartZ=0 EndX=-3.05 EndY=0 EndZ=0
  constraints (23):
    c: PointOnObject(g0,g-1)
    c: PointOnObject(g1,g-1)
    c: PointOnObject(g0,g-1)
    c: Coincident(g2,g0)
    c: Vertical(g2)
    c: Coincident(g3,g2)
    c: Horizontal(g3)
    c: Coincident(g4,g3)
    c: Coincident(g4,g1)
    c: Vertical(g4)
    c: Coincident(g5,g1)
    c: Vertical(g5)
    c: Coincident(g6,g5)
    c: Horizontal(g6)
    c: Coincident(g7,g6)
    c: Coincident(g7,g0)
    c: Vertical(g7)
    c: Equal(g0,g1)
    c: Symmetric(g0,g1,g-1)
    c: Distance(g4) = 5.1
    c: Distance(g6) = 6.1
    c: Distance(g3) = 10
    c: Distance(g7) = 1
FEATURE [PartDesign::Pad] Pad010
  Direction = (1,1,1)
  Length = 8.1
  Length2 = 100
  Profile = -> Sketch022
  Type = 0
FEATURE [Sketcher::SketchObject] Sketch021
  FullyConstrained = true
  MapMode = 5
  Placement = pos=(0,0,8.1) rot=(0,0,1;0rad)
  Support = -> [Pad010]
  sketch-geometry (10):
    g0: LineSegment StartX=-4.45 StartY=0.55 StartZ=0 EndX=-3.45 EndY=0.55 EndZ=0
    g1: LineSegment StartX=-3.45 StartY=0.55 StartZ=0 EndX=-3.45 EndY=1.55 EndZ=0
    g2: LineSegment StartX=-3.45 StartY=1.55 StartZ=0 EndX=3.45 EndY=1.55 EndZ=0
    g3: LineSegment StartX=3.45 StartY=1.55 StartZ=0 EndX=3.45 EndY=0.55 EndZ=0
    g4: LineSegment StartX=3.45 StartY=0.55 StartZ=0 EndX=4.45 EndY=0.55 EndZ=0
    g5: LineSegment StartX=4.45 StartY=0.55 StartZ=0 EndX=4.45 EndY=4.55 EndZ=0
    g6: LineSegment StartX=4.45 StartY=4.55 StartZ=0 EndX=-4.45 EndY=4.55 EndZ=0
    g7: LineSegment StartX=-4.45 StartY=4.55 StartZ=0 EndX=-4.45 EndY=0.55 EndZ=0
    g8: LineSegment StartX=-3.45 StartY=0.55 StartZ=0 EndX=3.45 EndY=0.55 EndZ=0
    g9: LineSegment StartX=0 StartY=0 StartZ=0 EndX=0 EndY=0.55 EndZ=0
  constraints (28):
    c: Horizontal(g0)
    c: Coincident(g1,g0)
    c: Coincident(g2,g1)
    c: Horizontal(g2)
    c: Coincident(g3,g2)
    c: Vertical(g3)
    c: Coincident(g4,g3)
    c: Horizontal(g4)
    c: Coincident(g5,g4)
    c: Vertical(g5)
    c: Coincident(g6,g5)
    c: Horizontal(g6)
    c: Coincident(g7,g6)
    c: Coincident(g7,g0)
    c: Vertical(g7)
    c: Vertical(g1)
    c: Coincident(g8,g0)
    c: Coincident(g8,g3)
    c: Horizontal(g8)
    c: Equal(g0,g4)
    c: Coincident(g9,g-1)
    c: PointOnObject(g9,g-2)
    c: Symmetric(g0,g3,g9)
    c: Distance(g0) = 1
    c: Distance(g1) = 1
    c: Distance(g9) = 0.55
    c: Distance(g6) = 8.9
    c: DistanceY(g2,g5) = 3
FEATURE [PartDesign::Pocket] Pocket007
  BaseFeature = -> Pad010
  Length = 7
  Length2 = 100
  Profile = -> Sketch021
  Type = 0
FEATURE [Sketcher::SketchObject] Sketch024
  FullyConstrained = true
  MapMode = 5
  Placement = pos=(0,0,8.1) rot=(0,0,1;0rad)
  Support = -> [Pocket007]
  sketch-geometry (5):
    g0: LineSegment StartX=0 StartY=0 StartZ=0 EndX=0 EndY=3 EndZ=0
    g1: LineSegment StartX=-3.4 StartY=8 StartZ=0 EndX=3.4 EndY=8 EndZ=0
    g2: LineSegment StartX=3.4 StartY=8 StartZ=0 EndX=3.4 EndY=3 EndZ=0
    g3: LineSegment StartX=3.4 StartY=3 StartZ=0 EndX=-3.4 EndY=3 EndZ=0
    g4: LineSegment StartX=-3.4 StartY=3 StartZ=0 EndX=-3.4 EndY=8 EndZ=0
  constraints (14):
    c: Coincident(g0,g-1)
    c: PointOnObject(g0,g-2)
    c: Coincident(g1,g2)
    c: Coincident(g2,g3)
    c: Coincident(g3,g4)
    c: Coincident(g4,g1)
    c: Horizontal(g1)
    c: Horizontal(g3)
    c: Vertical(g2)
    c: Vertical(g4)
    c: Symmetric(g3,g2,g0)
    c: Distance(g0) = 3
    c: Distance(g2) = 5
    c: Distance(g1) = 6.8
FEATURE [PartDesign::Pocket] Pocket009
  BaseFeature = -> Pocket007
  Length = 1
  Length2 = 100
  Profile = -> Sketch024
  Type = 0
FEATURE [Sketcher::SketchObject] Sketch018
  FullyConstrained = true
  MapMode = 5
  Placement = pos=(0,0,8.1) rot=(0,0,1;0rad)
  Support = -> [Pocket009]
  sketch-geometry (4):
    g0: LineSegment StartX=-2.75 StartY=3 StartZ=0 EndX=2.75 EndY=3 EndZ=0
    g1: LineSegment StartX=2.75 StartY=3 StartZ=0 EndX=2.75 EndY=0 EndZ=0
    g2: LineSegment StartX=2.75 StartY=0 StartZ=0 EndX=-2.75 EndY=0 EndZ=0
    g3: LineSegment StartX=-2.75 StartY=0 StartZ=0 EndX=-2.75 EndY=3 EndZ=0
  constraints (11):
    c: Coincident(g0,g1)
    c: Coincident(g1,g2)
    c: Coincident(g2,g3)
    c: Coincident(g3,g0)
    c: Horizontal(g0)
    c: Horizontal(g2)
    c: Vertical(g1)
    c: Vertical(g3)
    c: Symmetric(g2,g1,g-1)
    c: Distance(g1) = 3
    c: Distance(g0) = 5.5
FEATURE [PartDesign::Pocket] Pocket010
  BaseFeature = -> Pocket009
  Length = 3
  Length2 = 100
  Profile = -> Sketch018
  Type = 0
FEATURE [Sketcher::SketchObject] Sketch023
  FullyConstrained = true
  MapMode = 5
  Placement = pos=(0,0,1.1) rot=(0,0,1;0rad)
  Support = -> [Pocket010]
  sketch-geometry (5):
    g0: ArcOfCircle CenterX=-3.4 CenterY=3 CenterZ=0 NormalX=0 NormalY=0 NormalZ=1 AngleXU=0 Radius=0.25 StartAngle=1.5708 EndAngle=4.71239
    g1: ArcOfCircle CenterX=3.4 CenterY=3 CenterZ=0 NormalX=0 NormalY=0 NormalZ=1 AngleXU=0 Radius=0.25 StartAngle=4.71239 EndAngle=7.85398
    g2: LineSegment StartX=-3.4 StartY=2.75 StartZ=0 EndX=3.4 EndY=2.75 EndZ=0
    g3: LineSegment StartX=-3.4 StartY=3.25 StartZ=0 EndX=3.4 EndY=3.25 EndZ=0
    g4: LineSegment StartX=0 StartY=0 StartZ=0 EndX=0 EndY=2.75 EndZ=0
  constraints (12):
    c: Tangent(g0,g3) = 1.5708
    c: Tangent(g0,g2) = -1.5708
    c: Tangent(g2,g1) = -1.5708
    c: Tangent(g3,g1) = 1.5708
    c: Horizontal(g2)
    c: Equal(g0,g1)
    c: Coincident(g4,g-1)
    c: PointOnObject(g4,g-2)
    c: Symmetric(g0,g1,g4)
    c: DistanceY(g-1,g1) = 3
    c: DistanceY(g1,g1) = 0.5
    c: DistanceX(g0,g1) = 6.8
FEATURE [PartDesign::Pad] Pad013
  BaseFeature = -> Pocket010
  Direction = (1,1,1)
  Length = 4
  Length2 = 100
  Profile = -> Sketch023
  Type = 0
FEATURE [PartDesign::Pad] Pad011
  BaseFeature = -> Pad013
  Direction = (1,1,1)
  Length = 3.4
  Length2 = 100
  Profile = -> Sketch019
  Reversed = true
  Type = 0
FEATURE [PartDesign::Body] Body014  label="GroveHeader007"
  Group = -> [Sketch022,Pad010,Sketch021,Pocket007,Sketch024,Pocket009,Sketch018,Pocket010,Sketch023,Pad013,Sketch019,Pad011]
  Origin = -> Origin020
  Placement = pos=(-13.8,0,1.6) rot=(0,0,1;1.5708rad)
  Tip = -> Pad011
FEATURE [PartDesign::FeatureBase] Clone006
  BaseFeature = -> Body014
  Placement = pos=(-14,0,1.6) rot=(0,0,1;1.5708rad)
FEATURE [PartDesign::Body] Body019  label="GroveHeader012"
  BaseFeature = -> Body014
  Group = -> [Clone006]
  Origin = -> Origin019
  Placement = pos=(6.4,0,0) rot=(0,0,1;0rad)
  Tip = -> Clone006
FEATURE [PartDesign::FeatureBase] Clone007
  BaseFeature = -> Body014
  Placement = pos=(-14,0,1.6) rot=(0,0,1;1.5708rad)
FEATURE [PartDesign::Body] Body015  label="GroveHeader008"
  BaseFeature = -> Body014
  Group = -> [Clone007]
  Origin = -> Origin023
  Placement = pos=(12.6,0,0) rot=(0,0,1;0rad)
  Tip = -> Clone007
FEATURE [PartDesign::FeatureBase] Clone008
  BaseFeature = -> Body014
  Placement = pos=(-14,0,1.6) rot=(0,0,1;1.5708rad)
FEATURE [PartDesign::Body] Body018  label="GroveHeader011"
  BaseFeature = -> Body014
  Group = -> [Clone008]
  Origin = -> Origin017
  Placement = pos=(31.2,0,0) rot=(0,0,1;0rad)
  Tip = -> Clone008
FEATURE [PartDesign::FeatureBase] Clone009
  BaseFeature = -> Body014
  Placement = pos=(-14,0,1.6) rot=(0,0,1;1.5708rad)
FEATURE [PartDesign::Body] Body016  label="GroveHeader009"
  BaseFeature = -> Body014
  Group = -> [Clone009]
  Origin = -> Origin016
  Placement = pos=(25,0,0) rot=(0,0,1;0rad)
  Tip = -> Clone009
FEATURE [PartDesign::FeatureBase] Clone010
  BaseFeature = -> Body014
  Placement = pos=(-14,0,1.6) rot=(0,0,1;1.5708rad)
FEATURE [PartDesign::Body] Body017  label="GroveHeader010"
  BaseFeature = -> Body014
  Group = -> [Clone010]
  Origin = -> Origin018
  Placement = pos=(18.8,0,0) rot=(0,0,1;0rad)
  Tip = -> Clone010
FEATURE [App::Part] Part003  label="Grove_I2CHub6_Part2"
  Group = -> [Body013,Body014,Body019,Body015,Body017,Body016,Body018]
  Origin = -> Origin022
  Placement = pos=(20.5,19,11) rot=(0,0,1;0rad)
FEATURE [Sketcher::SketchObject] Sketch025  label="Sketch_USMtHoles"
  FullyConstrained = true
  MapMode = 5
  Placement = pos=(0,0,0) rot=(1,0,0;1.5708rad)
  Support = -> [XZ_Plane001]
  expr: Constraints[17] = <<params>>.m2_hole_clear_diam
  expr: Constraints[9] = <<params>>.usr_mt_hole_width_short
  expr: Constraints[16] = <<params>>.usr_mt_hole_cent_loc_z
  expr: Constraints[8] = <<params>>.usr_mt_hole_height
  expr: Constraints[18] = <<params>>.usr_mt_hole_width_long
  expr: Constraints[30] = <<params>>.usr_mt_hole_width_short
  sketch-geometry (15):
    g0: LineSegment StartX=-22.625 StartY=37.25 StartZ=0 EndX=7.125 EndY=37.25 EndZ=0
    g1: LineSegment StartX=7.125 StartY=37.25 StartZ=0 EndX=7.125 EndY=16.75 EndZ=0
    g2: LineSegment StartX=7.125 StartY=16.75 StartZ=0 EndX=-22.625 EndY=16.75 EndZ=0
    g3: LineSegment StartX=-22.625 StartY=16.75 StartZ=0 EndX=-22.625 EndY=37.25 EndZ=0
    g4: GeomPoint X=7.125 Y=27 Z=0
    g5: Circle CenterX=-22.625 CenterY=27 CenterZ=0 NormalX=0 NormalY=0 NormalZ=1 AngleXU=0 Radius=1.25
    g6: Circle CenterX=7.125 CenterY=37.25 CenterZ=0 NormalX=0 NormalY=0 NormalZ=1 AngleXU=0 Radius=1.25
    g7: Circle CenterX=7.125 CenterY=16.75 CenterZ=0 NormalX=0 NormalY=0 NormalZ=1 AngleXU=0 Radius=1.25
    g8: LineSegment StartX=-7.125 StartY=37.25 StartZ=0 EndX=22.625 EndY=37.25 EndZ=0
    g9: LineSegment StartX=22.625 StartY=37.25 StartZ=0 EndX=22.625 EndY=16.75 EndZ=0
    g10: LineSegment StartX=22.625 StartY=16.75 StartZ=0 EndX=-7.125 EndY=16.75 EndZ=0
    g11: LineSegment StartX=-7.125 StartY=16.75 StartZ=0 EndX=-7.125 EndY=37.25 EndZ=0
    g12: Circle CenterX=-7.125 CenterY=37.25 CenterZ=0 NormalX=0 NormalY=0 NormalZ=1 AngleXU=0 Radius=1.25
    g13: Circle CenterX=-7.125 CenterY=16.75 CenterZ=0 NormalX=0 NormalY=0 NormalZ=1 AngleXU=0 Radius=1.25
    g14: Circle CenterX=22.625 CenterY=27 CenterZ=0 NormalX=0 NormalY=0 NormalZ=1 AngleXU=0 Radius=1.25
  constraints (37):
    c: Coincident(g0,g1)
    c: Coincident(g1,g2)
    c: Coincident(g2,g3)
    c: Coincident(g3,g0)
    c: Horizontal(g0)
    c: Horizontal(g2)
    c: Vertical(g1)
    c: Vertical(g3)
    c: DistanceY(g1,g0) = 20.5
    c: DistanceX(g-1,g1) = 7.125
    c: Symmetric(g1,g0,g4)
    c: Coincident(g6,g0)
    c: Coincident(g7,g1)
    c: Equal(g6,g5)
    c: Equal(g5,g7)
    c: Symmetric(g2,g0,g5)
    c: DistanceY(g-1,g4) = 27
    c: Diameter(g7) = 2.5
    c: DistanceX(g5,g-1) = 22.625
    c: Coincident(g8,g9)
    c: Coincident(g9,g10)
    c: Coincident(g10,g11)
    c: Coincident(g11,g8)
    c: Horizontal(g8)
    c: Horizontal(g10)
    c: Vertical(g9)
    c: Vertical(g11)
    c: PointOnObject(g8,g0)
    c: PointOnObject(g10,g2)
    c: Equal(g8,g0)
    c: DistanceX(g10,g-1) = 7.125
    c: Coincident(g12,g8)
    c: Coincident(g13,g10)
    c: Symmetric(g8,g9,g14)
    c: Equal(g6,g12)
    c: Equal(g13,g7)
    c: Equal(g7,g14)
FEATURE [PartDesign::Pocket] Pocket011  label="USMtHoles"
  BaseFeature = -> Pad009
  Length = 5
  Length2 = 100
  Placement = pos=(0,0,0) rot=(0.57735,0.57735,0.57735;2.0944rad)
  Profile = -> Sketch025
  Type = 1
FEATURE [Sketcher::SketchObject] Sketch026
  FullyConstrained = true
  MapMode = 5
  Placement = pos=(0,0,0) rot=(1,0,0;1.5708rad)
  Support = -> [XZ_Plane001]
  expr: Constraints[18] = <<params>>.i2c_mt_plate_height - 3mm
  expr: Constraints[2] = <<params>>.usr_mt_fr_arch_width
  expr: Constraints[16] = <<params>>.usr_mt_fr_arch_vert_height
  sketch-geometry (7):
    g0: LineSegment StartX=-13.5 StartY=0 StartZ=0 EndX=13.5 EndY=0 EndZ=0
    g1: LineSegment StartX=-13.5 StartY=0 StartZ=0 EndX=-13.5 EndY=3 EndZ=0
    g2: LineSegment StartX=13.5 StartY=0 StartZ=0 EndX=13.5 EndY=3 EndZ=0
    g3: LineSegment StartX=-13.5 StartY=3 StartZ=0 EndX=-9.3045 EndY=8 EndZ=0
    g4: LineSegment StartX=13.5 StartY=3 StartZ=0 EndX=9.3045 EndY=8 EndZ=0
    g5: LineSegment StartX=-9.3045 StartY=8 StartZ=0 EndX=9.3045 EndY=8 EndZ=0
    g6: LineSegment StartX=-13.5 StartY=3 StartZ=0 EndX=13.5 EndY=3 EndZ=0
  constraints (19):
    c: Horizontal(g0)
    c: Symmetric(g0,g0,g-1)
    c: DistanceX(g0,g0) = 27
    c: Coincident(g1,g0)
    c: Vertical(g1)
    c: Coincident(g2,g0)
    c: Vertical(g2)
    c: Coincident(g3,g1)
    c: Coincident(g4,g2)
    c: Coincident(g5,g3)
    c: Coincident(g5,g4)
    c: Horizontal(g5)
    c: Coincident(g6,g1)
    c: Coincident(g6,g2)
    c: Horizontal(g6)
    c: Angle(g4,g6) = 0.872665
    c: DistanceY(g0,g2) = 3
    c: Equal(g4,g3)
    c: DistanceY(g0,g4) = 8
FEATURE [PartDesign::Pocket] Pocket012  label="ArchCut"
  BaseFeature = -> Pocket011
  Length = 5
  Length2 = 100
  Placement = pos=(0,0,0) rot=(0.57735,0.57735,0.57735;2.0944rad)
  Profile = -> Sketch026
  Type = 1
FEATURE [PartDesign::Plane] DatumPlane  label="Datum_USHSunk"
  AttachmentOffset = pos=(0,0,-2) rot=(0,0,1;0rad)
  Length = 63.761
  MapMode = 5
  Placement = pos=(0,2,4e-16) rot=(1,0,0;1.5708rad)
  ResizeMode = 0
  Support = -> [XZ_Plane001]
  Width = 78.261
  expr: .AttachmentOffset.Base.z = -1 * <<params>>.usr_mt_csunk_offset
FEATURE [PartDesign::Plane] DatumPlane001  label="Datum_I2CMt_Surf"
  AttachmentOffset = pos=(0,0,11) rot=(0,0,1;0rad)
  Length = 62.8885
  MapMode = 5
  Placement = pos=(0,0,11) rot=(0,0,1;0rad)
  ResizeMode = 0
  Support = -> [XY_Plane001]
  Width = 67.8885
  expr: .AttachmentOffset.Base.z = <<params>>.i2c_mt_plate_height
FEATURE [PartDesign::Plane] DatumPlane002  label="Datum_ToPlate_CSunk"
  AttachmentOffset = pos=(0,0,2) rot=(0,0,1;0rad)
  Length = 62.8885
  MapMode = 5
  Placement = pos=(0,0,2) rot=(0,0,1;0rad)
  ResizeMode = 0
  Support = -> [XY_Plane001]
  Width = 67.8885
  expr: .AttachmentOffset.Base.z = <<params>>.mt_to_plate_csunk_z
FEATURE [PartDesign::Plane] DatumPlane003  label="Datum_ToPlate_Slot"
  AttachmentOffset = pos=(0,0,4) rot=(0,0,1;0rad)
  Length = 62.8885
  MapMode = 5
  Placement = pos=(0,0,4) rot=(0,0,1;0rad)
  ResizeMode = 0
  Support = -> [XY_Plane001]
  Width = 67.8885
  expr: .AttachmentOffset.Base.z = <<params>>.mt_to_plate_slot_z
FEATURE [PartDesign::Plane] DatumPlane004  label="Datum_I2CMt_Slot"
  AttachmentOffset = pos=(0,0,9) rot=(0,0,1;0rad)
  Length = 62.8885
  MapMode = 5
  Placement = pos=(0,0,9) rot=(0,0,1;0rad)
  ResizeMode = 0
  Support = -> [XY_Plane001]
  Width = 67.8885
  expr: .AttachmentOffset.Base.z = <<params>>.i2c_mt_slot_z
FEATURE [PartDesign::Plane] DatumPlane005  label="Datum_I2CMt_CSunk"
  AttachmentOffset = pos=(0,0,9) rot=(0,0,1;0rad)
  Length = 62.8885
  MapMode = 5
  Placement = pos=(0,0,9) rot=(0,0,1;0rad)
  ResizeMode = 0
  Support = -> [XY_Plane001]
  Width = 67.8885
  expr: .AttachmentOffset.Base.z = <<params>>.i2c_mt_csunk_z
FEATURE [Sketcher::SketchObject] Sketch027  label="Sketch_I2CMtHoles_Temp"
  FullyConstrained = true
  MapMode = 5
  Support = -> [XY_Plane001]
  expr: Constraints[20] = <<params>>.i2c_mt_holes_offset_leng
  expr: Constraints[21] = <<params>>.i2c_mt_holes_length
  expr: Constraints[19] = <<params>>.i2c_mt_holes_width
  sketch-geometry (8):
    g0: LineSegment StartX=-10.5 StartY=29 StartZ=0 EndX=10.5 EndY=29 EndZ=0
    g1: LineSegment StartX=10.5 StartY=29 StartZ=0 EndX=10.5 EndY=9 EndZ=0
    g2: LineSegment StartX=10.5 StartY=9 StartZ=0 EndX=-10.5 EndY=9 EndZ=0
    g3: LineSegment StartX=-10.5 StartY=9 StartZ=0 EndX=-10.5 EndY=29 EndZ=0
    g4: LineSegment StartX=0 StartY=0 StartZ=0 EndX=2e-16 EndY=0 EndZ=0
    g5: LineSegment StartX=2e-16 StartY=0 StartZ=0 EndX=2e-16 EndY=9 EndZ=0
    g6: LineSegment StartX=2e-16 StartY=9 StartZ=0 EndX=0 EndY=9 EndZ=0
    g7: LineSegment StartX=0 StartY=9 StartZ=0 EndX=0 EndY=0 EndZ=0
  constraints (22):
    c: Coincident(g0,g1)
    c: Coincident(g1,g2)
    c: Coincident(g2,g3)
    c: Coincident(g3,g0)
    c: Horizontal(g0)
    c: Horizontal(g2)
    c: Vertical(g1)
    c: Vertical(g3)
    c: Coincident(g4,g5)
    c: Coincident(g5,g6)
    c: Coincident(g6,g7)
    c: Coincident(g7,g4)
    c: Horizontal(g4)
    c: Horizontal(g6)
    c: Vertical(g5)
    c: Vertical(g7)
    c: Coincident(g4,g-1)
    c: PointOnObject(g5,g-2)
    c: Symmetric(g2,g1,g5)
    c: DistanceX(g2,g1) = 21
    c: DistanceY(g-1,g1) = 9
    c: DistanceY(g1,g0) = 20
FEATURE [Sketcher::SketchObject] Sketch030  label="Sketch_MtToPlateHoles_Temp"
  FullyConstrained = true
  MapMode = 5
  Support = -> [XY_Plane001]
  expr: Constraints[4] = <<params>>.mt_to_plate_hole_loc_l
  expr: Constraints[5] = <<params>>.mt_to_plate_hole_space_w
  sketch-geometry (2):
    g0: LineSegment StartX=-20 StartY=26 StartZ=0 EndX=20 EndY=26 EndZ=0
    g1: LineSegment StartX=0 StartY=0 StartZ=0 EndX=0 EndY=26 EndZ=0
  constraints (6):
    c: Horizontal(g0)
    c: Coincident(g1,g-1)
    c: PointOnObject(g1,g-2)
    c: Symmetric(g0,g0,g1)
    c: DistanceY(g-1,g1) = 26
    c: DistanceX(g0,g0) = 40
FEATURE [Sketcher::SketchObject] Sketch031  label="Sketch_MtToPlateHoles"
  FullyConstrained = true
  MapMode = 5
  Support = -> [XY_Plane001]
  expr: Constraints[19] = <<params>>.mt_to_plate_hole_offset_l
  expr: Constraints[5] = <<params>>.mt_to_plate_hole_space_w
  expr: Constraints[4] = <<params>>.mt_to_plate_hole_loc_l
  expr: Constraints[9] = <<params>>.m25_hole_clear_diam
  sketch-geometry (8):
    g0: LineSegment StartX=-20 StartY=26 StartZ=0 EndX=20 EndY=26 EndZ=0
    g1: LineSegment StartX=0 StartY=0 StartZ=0 EndX=0 EndY=26 EndZ=0
    g2: Circle CenterX=-20 CenterY=26 CenterZ=0 NormalX=0 NormalY=0 NormalZ=1 AngleXU=0 Radius=1.4
    g3: Circle CenterX=20 CenterY=26 CenterZ=0 NormalX=0 NormalY=0 NormalZ=1 AngleXU=0 Radius=1.4
    g4: LineSegment StartX=-20 StartY=26 StartZ=0 EndX=-20 EndY=5 EndZ=0
    g5: LineSegment StartX=20 StartY=26 StartZ=0 EndX=20 EndY=5 EndZ=0
    g6: Circle CenterX=-20 CenterY=5 CenterZ=0 NormalX=0 NormalY=0 NormalZ=1 AngleXU=0 Radius=1.4
    g7: Circle CenterX=20 CenterY=5 CenterZ=0 NormalX=0 NormalY=0 NormalZ=1 AngleXU=0 Radius=1.4
  constraints (20):
    c: Horizontal(g0)
    c: Coincident(g1,g-1)
    c: PointOnObject(g1,g-2)
    c: Symmetric(g0,g0,g1)
    c: DistanceY(g-1,g1) = 26
    c: DistanceX(g0,g0) = 40
    c: Coincident(g2,g0)
    c: Coincident(g3,g0)
    c: Equal(g3,g2)
    c: Diameter(g3) = 2.8
    c: Coincident(g4,g2)
    c: Vertical(g4)
    c: Coincident(g5,g3)
    c: Vertical(g5)
    c: Equal(g4,g5)
    c: Coincident(g6,g4)
    c: Coincident(g7,g5)
    c: Equal(g7,g3)
    c: Equal(g7,g6)
    c: DistanceY(g-1,g7) = 5
FEATURE [PartDesign::Pocket] Pocket015  label="MtToPlateHoles"
  BaseFeature = -> Pocket012
  Length = 9
  Length2 = 100
  Placement = pos=(0,0,0) rot=(0.57735,0.57735,0.57735;2.0944rad)
  Profile = -> Sketch031
  Reversed = true
  Type = 0
  expr: Length = <<params>>.i2c_mt_plate_height - 2mm
FEATURE [Sketcher::SketchObject] Sketch032  label="Sketch_MtToPlateCSunk"
  FullyConstrained = true
  MapMode = 5
  Placement = pos=(0,0,2) rot=(0,0,1;0rad)
  Support = -> [DatumPlane002]
  expr: Constraints[91] = <<params>>.mt_to_plate_hole_offset_l
  expr: Constraints[5] = <<params>>.mt_to_plate_hole_space_w
  expr: Constraints[4] = <<params>>.mt_to_plate_hole_loc_l
  expr: Constraints[45] = <<params>>.m25_nut_clear_flat
  sketch-geometry (32):
    g0: LineSegment StartX=-20 StartY=26 StartZ=0 EndX=20 EndY=26 EndZ=0
    g1: LineSegment StartX=0 StartY=0 StartZ=0 EndX=0 EndY=26 EndZ=0
    g2: LineSegment StartX=-20 StartY=29.0022 StartZ=0 EndX=-22.6 EndY=27.5011 EndZ=0
    g3: LineSegment StartX=-22.6 StartY=27.5011 StartZ=0 EndX=-22.6 EndY=24.4989 EndZ=0
    g4: LineSegment StartX=-22.6 StartY=24.4989 StartZ=0 EndX=-20 EndY=22.9978 EndZ=0
    g5: LineSegment StartX=-20 StartY=22.9978 StartZ=0 EndX=-17.4 EndY=24.4989 EndZ=0
    g6: LineSegment StartX=-17.4 StartY=24.4989 StartZ=0 EndX=-17.4 EndY=27.5011 EndZ=0
    g7: LineSegment StartX=-17.4 StartY=27.5011 StartZ=0 EndX=-20 EndY=29.0022 EndZ=0
    g8: Circle CenterX=-20 CenterY=26 CenterZ=0 NormalX=0 NormalY=0 NormalZ=1 AngleXU=0 Radius=3.00222
    g9: LineSegment StartX=20 StartY=29.0022 StartZ=0 EndX=17.4 EndY=27.5011 EndZ=0
    g10: LineSegment StartX=17.4 StartY=27.5011 StartZ=0 EndX=17.4 EndY=24.4989 EndZ=0
    g11: LineSegment StartX=17.4 StartY=24.4989 StartZ=0 EndX=20 EndY=22.9978 EndZ=0
    g12: LineSegment StartX=20 StartY=22.9978 StartZ=0 EndX=22.6 EndY=24.4989 EndZ=0
    g13: LineSegment StartX=22.6 StartY=24.4989 StartZ=0 EndX=22.6 EndY=27.5011 EndZ=0
    g14: LineSegment StartX=22.6 StartY=27.5011 StartZ=0 EndX=20 EndY=29.0022 EndZ=0
    g15: Circle CenterX=20 CenterY=26 CenterZ=0 NormalX=0 NormalY=0 NormalZ=1 AngleXU=0 Radius=3.00222
    g16: LineSegment StartX=-20 StartY=26 StartZ=0 EndX=-20 EndY=5 EndZ=0
    g17: LineSegment StartX=20 StartY=26 StartZ=0 EndX=20 EndY=5 EndZ=0
    g18: LineSegment StartX=-20 StartY=8.00222 StartZ=0 EndX=-22.6 EndY=6.50111 EndZ=0
    g19: LineSegment StartX=-22.6 StartY=6.50111 StartZ=0 EndX=-22.6 EndY=3.49889 EndZ=0
    g20: LineSegment StartX=-22.6 StartY=3.49889 StartZ=0 EndX=-20 EndY=1.99778 EndZ=0
    g21: LineSegment StartX=-20 StartY=1.99778 StartZ=0 EndX=-17.4 EndY=3.49889 EndZ=0
    g22: LineSegment StartX=-17.4 StartY=3.49889 StartZ=0 EndX=-17.4 EndY=6.50111 EndZ=0
    g23: LineSegment StartX=-17.4 StartY=6.50111 StartZ=0 EndX=-20 EndY=8.00222 EndZ=0
    g24: Circle CenterX=-20 CenterY=5 CenterZ=0 NormalX=0 NormalY=0 NormalZ=1 AngleXU=0 Radius=3.00222
    g25: LineSegment StartX=20 StartY=8.00222 StartZ=0 EndX=17.4 EndY=6.50111 EndZ=0
    g26: LineSegment StartX=17.4 StartY=6.50111 StartZ=0 EndX=17.4 EndY=3.49889 EndZ=0
    g27: LineSegment StartX=17.4 StartY=3.49889 StartZ=0 EndX=20 EndY=1.99778 EndZ=0
    g28: LineSegment StartX=20 StartY=1.99778 StartZ=0 EndX=22.6 EndY=3.49889 EndZ=0
    g29: LineSegment StartX=22.6 StartY=3.49889 StartZ=0 EndX=22.6 EndY=6.50111 EndZ=0
    g30: LineSegment StartX=22.6 StartY=6.50111 StartZ=0 EndX=20 EndY=8.00222 EndZ=0
    g31: Circle CenterX=20 CenterY=5 CenterZ=0 NormalX=0 NormalY=0 NormalZ=1 AngleXU=0 Radius=3.00222
  constraints (76):
    c: Horizontal(g0)
    c: Coincident(g1,g-1)
    c: PointOnObject(g1,g-2)
    c: Symmetric(g0,g0,g1)
    c: DistanceY(g-1,g1) = 26
    c: DistanceX(g0,g0) = 40
    c: Coincident(g2,g3)
    c: Coincident(g3,g4)
    c: Coincident(g4,g5)
    c: Coincident(g5,g6)
    c: Coincident(g6,g7)
    c: Coincident(g7,g2)
    c: Equal(g2, g3-g7) x5
    c: PointOnObject(g2,g8)
    c: PointOnObject(g3,g8)
    c: PointOnObject(g4,g8)
    c: PointOnObject(g5,g8)
    c: PointOnObject(g6,g8)
    c: PointOnObject(g7,g8)
    c: Coincident(g8,g0)
    c: Coincident(g9,g10)
    c: Coincident(g10,g11)
    c: Coincident(g11,g12)
    c: Coincident(g12,g13)
    c: Coincident(g13,g14)
    c: Coincident(g14,g9)
    c: Equal(g9, g10-g14) x5
    c: PointOnObject(g9,g15)
    c: PointOnObject(g10,g15)
    c: PointOnObject(g11,g15)
    c: PointOnObject(g12,g15)
    c: PointOnObject(g13,g15)
    c: PointOnObject(g14,g15)
    c: Coincident(g15,g0)
    c: Vertical(g6)
    c: Vertical(g10)
    c: Equal(g15,g8)
    c: DistanceX(g10,g12) = 5.2
    c: Coincident(g16,g0)
    c: Vertical(g16)
    c: Coincident(g17,g0)
    c: Vertical(g17)
    c: Coincident(g18,g19)
    c: Coincident(g19,g20)
    c: Coincident(g20,g21)
    c: Coincident(g21,g22)
    c: Coincident(g22,g23)
    c: Coincident(g23,g18)
    c: Equal(g18, g19-g23) x5
    c: PointOnObject(g18,g24)
    c: PointOnObject(g19,g24)
    c: PointOnObject(g20,g24)
    c: PointOnObject(g21,g24)
    c: PointOnObject(g22,g24)
    c: PointOnObject(g23,g24)
    c: Coincident(g24,g16)
    c: PointOnObject(g23,g16)
    c: Coincident(g25,g26)
    c: Coincident(g26,g27)
    c: Coincident(g27,g28)
    c: Coincident(g28,g29)
    c: Coincident(g29,g30)
    c: Coincident(g30,g25)
    c: Equal(g25, g26-g30) x5
    c: PointOnObject(g25,g31)
    c: PointOnObject(g26,g31)
    c: PointOnObject(g27,g31)
    c: PointOnObject(g28,g31)
    c: PointOnObject(g29,g31)
    c: PointOnObject(g30,g31)
    c: Coincident(g31,g17)
    c: PointOnObject(g30,g17)
    c: Equal(g17,g16)
    c: Equal(g31,g15)
    c: Equal(g31,g24)
    c: DistanceY(g-1,g17) = 5
FEATURE [PartDesign::Pocket] Pocket016  label="MtToPlateCSunk"
  BaseFeature = -> Pocket015
  Length = 2
  Length2 = 100
  Placement = pos=(0,0,0) rot=(0.57735,0.57735,0.57735;2.0944rad)
  Profile = -> Sketch032
  Reversed = true
  Type = 0
  expr: Length = <<params>>.m25_nut_min_depth
FEATURE [Sketcher::SketchObject] Sketch033  label="Sketch_MtToPlateSlot"
  FullyConstrained = true
  MapMode = 5
  Placement = pos=(0,0,4) rot=(0,0,1;0rad)
  Support = -> [DatumPlane003]
  expr: Constraints[87] = <<params>>.mt_to_plate_hole_offset_l
  expr: Constraints[4] = <<params>>.mt_to_plate_hole_loc_l
  expr: Constraints[5] = <<params>>.mt_to_plate_hole_space_w
  expr: Constraints[35] = <<params>>.m25_nut_clear_flat
  sketch-geometry (37):
    g0: LineSegment StartX=-20 StartY=26 StartZ=0 EndX=20 EndY=26 EndZ=0
    g1: LineSegment StartX=0 StartY=0 StartZ=0 EndX=0 EndY=26 EndZ=0
    g2: LineSegment StartX=-20 StartY=22.9978 StartZ=0 EndX=-17.4 EndY=24.4989 EndZ=0
    g3: LineSegment StartX=-17.4 StartY=24.4989 StartZ=0 EndX=-17.4 EndY=27.5011 EndZ=0
    g4: LineSegment StartX=-22.6 StartY=27.5011 StartZ=0 EndX=-22.6 EndY=24.4989 EndZ=0
    g5: LineSegment StartX=-22.6 StartY=24.4989 StartZ=0 EndX=-20 EndY=22.9978 EndZ=0
    g6: Circle CenterX=-20 CenterY=26 CenterZ=0 NormalX=0 NormalY=0 NormalZ=1 AngleXU=0 Radius=3.00222
    g7: LineSegment StartX=20 StartY=22.9978 StartZ=0 EndX=22.6 EndY=24.4989 EndZ=0
    g8: LineSegment StartX=22.6 StartY=24.4989 StartZ=0 EndX=22.6 EndY=27.5011 EndZ=0
    g9: LineSegment StartX=17.4 StartY=27.5011 StartZ=0 EndX=17.4 EndY=24.4989 EndZ=0
    g10: LineSegment StartX=17.4 StartY=24.4989 StartZ=0 EndX=20 EndY=22.9978 EndZ=0
    g11: Circle CenterX=20 CenterY=26 CenterZ=0 NormalX=0 NormalY=0 NormalZ=1 AngleXU=0 Radius=3.00222
    g12: LineSegment StartX=17.4 StartY=27.5011 StartZ=0 EndX=17.4 EndY=47.5011 EndZ=0
    g13: LineSegment StartX=22.6 StartY=27.5011 StartZ=0 EndX=22.6 EndY=47.5011 EndZ=0
    g14: LineSegment StartX=17.4 StartY=47.5011 StartZ=0 EndX=22.6 EndY=47.5011 EndZ=0
    g15: LineSegment StartX=-22.6 StartY=27.5011 StartZ=0 EndX=-22.6 EndY=47.5011 EndZ=0
    g16: LineSegment StartX=-17.4 StartY=27.5011 StartZ=0 EndX=-17.4 EndY=47.5011 EndZ=0
    g17: LineSegment StartX=-22.6 StartY=47.5011 StartZ=0 EndX=-17.4 EndY=47.5011 EndZ=0
    g18: LineSegment StartX=-17.4 StartY=47.5011 StartZ=0 EndX=17.4 EndY=47.5011 EndZ=0
    g19: LineSegment StartX=-20 StartY=26 StartZ=0 EndX=-20 EndY=5 EndZ=0
    g20: LineSegment StartX=20 StartY=26 StartZ=0 EndX=20 EndY=5 EndZ=0
    g21: LineSegment StartX=-20 StartY=8.00222 StartZ=0 EndX=-22.6 EndY=6.50111 EndZ=0
    g22: LineSegment StartX=-22.6 StartY=6.50111 StartZ=0 EndX=-22.6 EndY=3.49889 EndZ=0
    g23: LineSegment StartX=-17.4 StartY=3.49889 StartZ=0 EndX=-17.4 EndY=6.50111 EndZ=0
    g24: LineSegment StartX=-17.4 StartY=6.50111 StartZ=0 EndX=-20 EndY=8.00222 EndZ=0
    g25: Circle CenterX=-20 CenterY=5 CenterZ=0 NormalX=0 NormalY=0 NormalZ=1 AngleXU=0 Radius=3.00222
    g26: LineSegment StartX=20 StartY=8.00222 StartZ=0 EndX=17.4 EndY=6.50111 EndZ=0
    g27: LineSegment StartX=17.4 StartY=6.50111 StartZ=0 EndX=17.4 EndY=3.49889 EndZ=0
    g28: LineSegment StartX=22.6 StartY=3.49889 StartZ=0 EndX=22.6 EndY=6.50111 EndZ=0
    g29: LineSegment StartX=22.6 StartY=6.50111 StartZ=0 EndX=20 EndY=8.00222 EndZ=0
    g30: Circle CenterX=20 CenterY=5 CenterZ=0 NormalX=0 NormalY=0 NormalZ=1 AngleXU=0 Radius=3.00222
    g31: LineSegment StartX=-22.6 StartY=3.49889 StartZ=0 EndX=-22.6 EndY=-16.5011 EndZ=0
    g32: LineSegment StartX=-17.4 StartY=3.49889 StartZ=0 EndX=-17.4 EndY=-16.5011 EndZ=0
    g33: LineSegment StartX=-22.6 StartY=-16.5011 StartZ=0 EndX=-17.4 EndY=-16.5011 EndZ=0
    g34: LineSegment StartX=22.6 StartY=3.49889 StartZ=0 EndX=22.6 EndY=-16.5011 EndZ=0
    g35: LineSegment StartX=17.4 StartY=3.49889 StartZ=0 EndX=17.4 EndY=-16.5011 EndZ=0
    g36: LineSegment StartX=17.4 StartY=-16.5011 StartZ=0 EndX=22.6 EndY=-16.5011 EndZ=0
  constraints (106):
    c: Horizontal(g0)
    c: Coincident(g1,g-1)
    c: PointOnObject(g1,g-2)
    c: Symmetric(g0,g0,g1)
    c: DistanceY(g-1,g1) = 26
    c: DistanceX(g0,g0) = 40
    c: Coincident(g2,g3)
    c: Coincident(g4,g5)
    c: Coincident(g5,g2)
    c: Equal(g2,g3)
    c: Equal(g2,g4)
    c: Equal(g2,g5)
    c: PointOnObject(g2,g6)
    c: PointOnObject(g3,g6)
    c: PointOnObject(g4,g6)
    c: PointOnObject(g4,g6)
    c: PointOnObject(g5,g6)
    c: Coincident(g6,g0)
    c: Coincident(g7,g8)
    c: Coincident(g9,g10)
    c: Coincident(g10,g7)
    c: Equal(g7,g8)
    c: Equal(g7,g9)
    c: Equal(g7,g10)
    c: PointOnObject(g7,g11)
    c: PointOnObject(g8,g11)
    c: PointOnObject(g9,g11)
    c: PointOnObject(g9,g11)
    c: PointOnObject(g10,g11)
    c: Coincident(g11,g0)
    c: Vertical(g4)
    c: Vertical(g8)
    c: Equal(g6,g11)
    c: Vertical(g9)
    c: Vertical(g3)
    c: DistanceX(g9,g7) = 5.2
    c: Coincident(g12,g9)
    c: Vertical(g12)
    c: Coincident(g13,g8)
    c: Vertical(g13)
    c: Coincident(g14,g12)
    c: Coincident(g14,g13)
    c: Horizontal(g14)
    c: Coincident(g15,g4)
    c: Vertical(g15)
    c: Coincident(g16,g3)
    c: Vertical(g16)
    c: Coincident(g17,g15)
    c: Coincident(g17,g16)
    c: Horizontal(g17)
    c: Coincident(g18,g16)
    c: Coincident(g18,g12)
    c: Horizontal(g18)
    c: Distance(g13) = 20
    c: Coincident(g19,g0)
    c: Vertical(g19)
    c: Coincident(g20,g0)
    c: Vertical(g20)
    c: Equal(g20,g19)
    c: Coincident(g21,g22)
    c: Coincident(g23,g24)
    c: Coincident(g24,g21)
    c: Equal(g21,g22)
    c: Equal(g21,g23)
    c: Equal(g21,g24)
    c: PointOnObject(g21,g25)
    c: PointOnObject(g22,g25)
    c: PointOnObject(g23,g25)
    c: PointOnObject(g23,g25)
    c: PointOnObject(g24,g25)
    c: Coincident(g25,g19)
    c: PointOnObject(g24,g19)
    c: Coincident(g26,g27)
    c: Coincident(g28,g29)
    c: Coincident(g29,g26)
    c: Equal(g26,g27)
    c: Equal(g26,g28)
    c: Equal(g26,g29)
    c: PointOnObject(g26,g30)
    c: PointOnObject(g27,g30)
    c: PointOnObject(g28,g30)
    c: PointOnObject(g28,g30)
    c: PointOnObject(g29,g30)
    c: Coincident(g30,g20)
    c: PointOnObject(g29,g20)
    c: Equal(g11,g30)
    c: Equal(g30,g25)
    c: DistanceY(g-1,g20) = 5
    c: Vertical(g28)
    c: Vertical(g22)
    c: Coincident(g31,g22)
    c: Vertical(g31)
    c: Coincident(g32,g23)
    c: Vertical(g32)
    c: Coincident(g33,g31)
    c: Coincident(g33,g32)
    c: Horizontal(g33)
    c: Equal(g15,g31)
    c: Coincident(g34,g28)
    c: Vertical(g34)
    c: Coincident(g35,g27)
    c: Vertical(g35)
    c: Coincident(g36,g35)
    c: Coincident(g36,g34)
    c: Horizontal(g36)
    c: Equal(g35,g31)
FEATURE [PartDesign::Pocket] Pocket017  label="MtToPlateSlot"
  BaseFeature = -> Pocket016
  Length = 2.5
  Length2 = 100
  Placement = pos=(0,0,0) rot=(0.57735,0.57735,0.57735;2.0944rad)
  Profile = -> Sketch033
  Reversed = true
  Type = 0
  expr: Length = <<params>>.mt_to_plate_slot_height
FEATURE [Sketcher::SketchObject] Sketch034  label="Sketch_I2CMtHoles"
  FullyConstrained = true
  MapMode = 5
  Support = -> [XY_Plane001]
  expr: Constraints[19] = <<params>>.i2c_mt_holes_width
  expr: Constraints[21] = <<params>>.i2c_mt_holes_length
  expr: Constraints[20] = <<params>>.i2c_mt_holes_offset_leng
  expr: Constraints[29] = <<params>>.m2_hole_clear_diam
  sketch-geometry (12):
    g0: LineSegment StartX=-10.5 StartY=29 StartZ=0 EndX=10.5 EndY=29 EndZ=0
    g1: LineSegment StartX=10.5 StartY=29 StartZ=0 EndX=10.5 EndY=9 EndZ=0
    g2: LineSegment StartX=10.5 StartY=9 StartZ=0 EndX=-10.5 EndY=9 EndZ=0
    g3: LineSegment StartX=-10.5 StartY=9 StartZ=0 EndX=-10.5 EndY=29 EndZ=0
    g4: LineSegment StartX=2e-16 StartY=0 StartZ=0 EndX=0 EndY=0 EndZ=0
    g5: LineSegment StartX=0 StartY=0 StartZ=0 EndX=0 EndY=9 EndZ=0
    g6: LineSegment StartX=0 StartY=9 StartZ=0 EndX=2e-16 EndY=9 EndZ=0
    g7: LineSegment StartX=2e-16 StartY=9 StartZ=0 EndX=2e-16 EndY=0 EndZ=0
    g8: Circle CenterX=-10.5 CenterY=29 CenterZ=0 NormalX=0 NormalY=0 NormalZ=1 AngleXU=0 Radius=1.25
    g9: Circle CenterX=10.5 CenterY=29 CenterZ=0 NormalX=0 NormalY=0 NormalZ=1 AngleXU=0 Radius=1.25
    g10: Circle CenterX=10.5 CenterY=9 CenterZ=0 NormalX=0 NormalY=0 NormalZ=1 AngleXU=0 Radius=1.25
    g11: Circle CenterX=-10.5 CenterY=9 CenterZ=0 NormalX=0 NormalY=0 NormalZ=1 AngleXU=0 Radius=1.25
  constraints (30):
    c: Coincident(g0,g1)
    c: Coincident(g1,g2)
    c: Coincident(g2,g3)
    c: Coincident(g3,g0)
    c: Horizontal(g0)
    c: Horizontal(g2)
    c: Vertical(g1)
    c: Vertical(g3)
    c: Coincident(g4,g5)
    c: Coincident(g5,g6)
    c: Coincident(g6,g7)
    c: Coincident(g7,g4)
    c: Horizontal(g4)
    c: Horizontal(g6)
    c: Vertical(g5)
    c: Vertical(g7)
    c: Coincident(g4,g-1)
    c: PointOnObject(g5,g-2)
    c: Symmetric(g2,g1,g5)
    c: DistanceX(g2,g1) = 21
    c: DistanceY(g-1,g1) = 9
    c: DistanceY(g1,g0) = 20
    c: Coincident(g8,g0)
    c: Coincident(g9,g0)
    c: Coincident(g10,g1)
    c: Coincident(g11,g2)
    c: Equal(g8,g9)
    c: Equal(g9,g10)
    c: Equal(g10,g11)
    c: Diameter(g9) = 2.5
FEATURE [PartDesign::Pocket] Pocket018  label="I2CMtHoles"
  BaseFeature = -> Pocket017
  Length = 5
  Length2 = 100
  Placement = pos=(0,0,0) rot=(0.57735,0.57735,0.57735;2.0944rad)
  Profile = -> Sketch034
  Reversed = true
  Type = 1
FEATURE [Sketcher::SketchObject] Sketch035  label="Sketch_I2CClearHoles"
  FullyConstrained = true
  MapMode = 5
  Placement = pos=(0,0,11) rot=(0,0,1;0rad)
  Support = -> [DatumPlane001]
  expr: Constraints[19] = <<params>>.i2c_mt_holes_width
  expr: Constraints[21] = <<params>>.i2c_mt_holes_length
  expr: Constraints[25] = <<params>>.i2c_plate_clear_diam
  expr: Constraints[20] = <<params>>.i2c_mt_holes_offset_leng
  sketch-geometry (10):
    g0: LineSegment StartX=-10.5 StartY=29 StartZ=0 EndX=10.5 EndY=29 EndZ=0
    g1: LineSegment StartX=10.5 StartY=29 StartZ=0 EndX=10.5 EndY=9 EndZ=0
    g2: LineSegment StartX=10.5 StartY=9 StartZ=0 EndX=-10.5 EndY=9 EndZ=0
    g3: LineSegment StartX=-10.5 StartY=9 StartZ=0 EndX=-10.5 EndY=29 EndZ=0
    g4: LineSegment StartX=2e-16 StartY=0 StartZ=0 EndX=0 EndY=0 EndZ=0
    g5: LineSegment StartX=0 StartY=0 StartZ=0 EndX=0 EndY=9 EndZ=0
    g6: LineSegment StartX=0 StartY=9 StartZ=0 EndX=2e-16 EndY=9 EndZ=0
    g7: LineSegment StartX=2e-16 StartY=9 StartZ=0 EndX=2e-16 EndY=0 EndZ=0
    g8: Circle CenterX=-10.5 CenterY=9 CenterZ=0 NormalX=0 NormalY=0 NormalZ=1 AngleXU=0 Radius=3
    g9: Circle CenterX=10.5 CenterY=9 CenterZ=0 NormalX=0 NormalY=0 NormalZ=1 AngleXU=0 Radius=3
  constraints (26):
    c: Coincident(g0,g1)
    c: Coincident(g1,g2)
    c: Coincident(g2,g3)
    c: Coincident(g3,g0)
    c: Horizontal(g0)
    c: Horizontal(g2)
    c: Vertical(g1)
    c: Vertical(g3)
    c: Coincident(g4,g5)
    c: Coincident(g5,g6)
    c: Coincident(g6,g7)
    c: Coincident(g7,g4)
    c: Horizontal(g4)
    c: Horizontal(g6)
    c: Vertical(g5)
    c: Vertical(g7)
    c: Coincident(g4,g-1)
    c: PointOnObject(g5,g-2)
    c: Symmetric(g2,g1,g5)
    c: DistanceX(g2,g1) = 21
    c: DistanceY(g-1,g1) = 9
    c: DistanceY(g1,g0) = 20
    c: Coincident(g8,g2)
    c: Coincident(g9,g1)
    c: Equal(g9,g8)
    c: Diameter(g9) = 6
FEATURE [PartDesign::Pocket] Pocket019  label="I2CClearHoles"
  BaseFeature = -> Pocket018
  Length = 5
  Length2 = 100
  Placement = pos=(0,0,0) rot=(0.57735,0.57735,0.57735;2.0944rad)
  Profile = -> Sketch035
  Reversed = true
  Type = 1
FEATURE [Sketcher::SketchObject] Sketch036  label="Sketch_I2CMtCSunk"
  FullyConstrained = true
  MapMode = 5
  Placement = pos=(0,0,9) rot=(0,0,1;0rad)
  Support = -> [DatumPlane005]
  expr: Constraints[117] = <<params>>.usr_mt_foot_width / 2
  expr: Constraints[19] = <<params>>.i2c_mt_holes_width
  expr: Constraints[101] = <<params>>.m2_nut_clear_flat
  expr: Constraints[21] = <<params>>.i2c_mt_holes_length
  expr: Constraints[20] = <<params>>.i2c_mt_holes_offset_leng
  sketch-geometry (42):
    g0: LineSegment StartX=-10.5 StartY=29 StartZ=0 EndX=10.5 EndY=29 EndZ=0
    g1: LineSegment StartX=10.5 StartY=29 StartZ=0 EndX=10.5 EndY=9 EndZ=0
    g2: LineSegment StartX=10.5 StartY=9 StartZ=0 EndX=-10.5 EndY=9 EndZ=0
    g3: LineSegment StartX=-10.5 StartY=9 StartZ=0 EndX=-10.5 EndY=29 EndZ=0
    g4: LineSegment StartX=0 StartY=0 StartZ=0 EndX=-1.6e-14 EndY=0 EndZ=0
    g5: LineSegment StartX=-1.6e-14 StartY=0 StartZ=0 EndX=-1.6e-14 EndY=9 EndZ=0
    g6: LineSegment StartX=-1.6e-14 StartY=9 StartZ=0 EndX=0 EndY=9 EndZ=0
    g7: LineSegment StartX=0 StartY=9 StartZ=0 EndX=0 EndY=0 EndZ=0
    g8: LineSegment StartX=-10.5 StartY=26.5751 StartZ=0 EndX=-8.4 EndY=27.7876 EndZ=0
    g9: LineSegment StartX=-8.4 StartY=27.7876 StartZ=0 EndX=-8.4 EndY=30.2124 EndZ=0
    g10: LineSegment StartX=-8.4 StartY=30.2124 StartZ=0 EndX=-10.5 EndY=31.4249 EndZ=0
    g11: LineSegment StartX=-10.5 StartY=31.4249 StartZ=0 EndX=-12.6 EndY=30.2124 EndZ=0
    g12: LineSegment StartX=-12.6 StartY=30.2124 StartZ=0 EndX=-12.6 EndY=27.7876 EndZ=0
    g13: LineSegment StartX=-12.6 StartY=27.7876 StartZ=0 EndX=-10.5 EndY=26.5751 EndZ=0
    g14: Circle CenterX=-10.5 CenterY=29 CenterZ=0 NormalX=0 NormalY=0 NormalZ=1 AngleXU=0 Radius=2.42487
    g15: LineSegment StartX=10.5 StartY=26.5751 StartZ=0 EndX=12.6 EndY=27.7876 EndZ=0
    g16: LineSegment StartX=12.6 StartY=27.7876 StartZ=0 EndX=12.6 EndY=30.2124 EndZ=0
    g17: LineSegment StartX=12.6 StartY=30.2124 StartZ=0 EndX=10.5 EndY=31.4249 EndZ=0
    g18: LineSegment StartX=10.5 StartY=31.4249 StartZ=0 EndX=8.4 EndY=30.2124 EndZ=0
    g19: LineSegment StartX=8.4 StartY=30.2124 StartZ=0 EndX=8.4 EndY=27.7876 EndZ=0
    g20: LineSegment StartX=8.4 StartY=27.7876 StartZ=0 EndX=10.5 EndY=26.5751 EndZ=0
    g21: Circle CenterX=10.5 CenterY=29 CenterZ=0 NormalX=0 NormalY=0 NormalZ=1 AngleXU=0 Radius=2.42487
    g22: LineSegment StartX=-10.5 StartY=11.4249 StartZ=0 EndX=-12.6 EndY=10.2124 EndZ=0
    g23: LineSegment StartX=-12.6 StartY=10.2124 StartZ=0 EndX=-12.6 EndY=7.78756 EndZ=0
    g24: LineSegment StartX=-12.6 StartY=7.78756 StartZ=0 EndX=-10.5 EndY=6.57513 EndZ=0
    g25: LineSegment StartX=-10.5 StartY=6.57513 StartZ=0 EndX=-8.4 EndY=7.78756 EndZ=0
    g26: LineSegment StartX=-8.4 StartY=7.78756 StartZ=0 EndX=-8.4 EndY=10.2124 EndZ=0
    g27: LineSegment StartX=-8.4 StartY=10.2124 StartZ=0 EndX=-10.5 EndY=11.4249 EndZ=0
    g28: Circle CenterX=-10.5 CenterY=9 CenterZ=0 NormalX=0 NormalY=0 NormalZ=1 AngleXU=0 Radius=2.42487
    g29: LineSegment StartX=10.5 StartY=11.4249 StartZ=0 EndX=8.4 EndY=10.2124 EndZ=0
    g30: LineSegment StartX=8.4 StartY=10.2124 StartZ=0 EndX=8.4 EndY=7.78756 EndZ=0
    g31: LineSegment StartX=8.4 StartY=7.78756 StartZ=0 EndX=10.5 EndY=6.57513 EndZ=0
    g32: LineSegment StartX=10.5 StartY=6.57513 StartZ=0 EndX=12.6 EndY=7.78756 EndZ=0
    g33: LineSegment StartX=12.6 StartY=7.78756 StartZ=0 EndX=12.6 EndY=10.2124 EndZ=0
    g34: LineSegment StartX=12.6 StartY=10.2124 StartZ=0 EndX=10.5 EndY=11.4249 EndZ=0
    g35: Circle CenterX=10.5 CenterY=9 CenterZ=0 NormalX=0 NormalY=0 NormalZ=1 AngleXU=0 Radius=2.42487
    g36: LineSegment StartX=-12.6 StartY=30.2124 StartZ=0 EndX=-12.6 EndY=46.2124 EndZ=0
    g37: LineSegment StartX=-8.4 StartY=30.2124 StartZ=0 EndX=-8.4 EndY=46.2124 EndZ=0
    g38: LineSegment StartX=-12.6 StartY=46.2124 StartZ=0 EndX=-8.4 EndY=46.2124 EndZ=0
    g39: LineSegment StartX=8.4 StartY=30.2124 StartZ=0 EndX=8.4 EndY=46.2124 EndZ=0
    g40: LineSegment StartX=12.6 StartY=30.2124 StartZ=0 EndX=12.6 EndY=46.2124 EndZ=0
    g41: LineSegment StartX=8.4 StartY=46.2124 StartZ=0 EndX=12.6 EndY=46.2124 EndZ=0
  constraints (102):
    c: Coincident(g0,g1)
    c: Coincident(g1,g2)
    c: Coincident(g2,g3)
    c: Coincident(g3,g0)
    c: Horizontal(g0)
    c: Horizontal(g2)
    c: Vertical(g1)
    c: Vertical(g3)
    c: Coincident(g4,g5)
    c: Coincident(g5,g6)
    c: Coincident(g6,g7)
    c: Coincident(g7,g4)
    c: Horizontal(g4)
    c: Horizontal(g6)
    c: Vertical(g5)
    c: Vertical(g7)
    c: Coincident(g4,g-1)
    c: PointOnObject(g5,g-2)
    c: Symmetric(g2,g1,g5)
    c: DistanceX(g2,g1) = 21
    c: DistanceY(g-1,g1) = 9
    c: DistanceY(g1,g0) = 20
    c: Coincident(g8,g9)
    c: Coincident(g9,g10)
    c: Coincident(g10,g11)
    c: Coincident(g11,g12)
    c: Coincident(g12,g13)
    c: Coincident(g13,g8)
    c: Equal(g8, g9-g13) x5
    c: PointOnObject(g8,g14)
    c: PointOnObject(g9,g14)
    c: PointOnObject(g10,g14)
    c: PointOnObject(g11,g14)
    c: PointOnObject(g12,g14)
    c: PointOnObject(g13,g14)
    c: Coincident(g14,g0)
    c: PointOnObject(g13,g3)
    c: Coincident(g15,g16)
    c: Coincident(g16,g17)
    c: Coincident(g17,g18)
    c: Coincident(g18,g19)
    c: Coincident(g19,g20)
    c: Coincident(g20,g15)
    c: Equal(g15, g16-g20) x5
    c: PointOnObject(g15,g21)
    c: PointOnObject(g16,g21)
    c: PointOnObject(g17,g21)
    c: PointOnObject(g18,g21)
    c: PointOnObject(g19,g21)
    c: PointOnObject(g20,g21)
    c: Coincident(g21,g0)
    c: PointOnObject(g20,g1)
    c: Coincident(g22,g23)
    c: Coincident(g23,g24)
    c: Coincident(g24,g25)
    c: Coincident(g25,g26)
    c: Coincident(g26,g27)
    c: Coincident(g27,g22)
    c: Equal(g22, g23-g27) x5
    c: PointOnObject(g22,g28)
    c: PointOnObject(g23,g28)
    c: PointOnObject(g24,g28)
    c: PointOnObject(g25,g28)
    c: PointOnObject(g26,g28)
    c: PointOnObject(g27,g28)
    c: Coincident(g28,g2)
    c: PointOnObject(g27,g3)
    c: Coincident(g29,g30)
    c: Coincident(g30,g31)
    c: Coincident(g31,g32)
    c: Coincident(g32,g33)
    c: Coincident(g33,g34)
    c: Coincident(g34,g29)
    c: Equal(g29, g30-g34) x5
    c: PointOnObject(g29,g35)
    c: PointOnObject(g30,g35)
    c: PointOnObject(g31,g35)
    c: PointOnObject(g32,g35)
    c: PointOnObject(g33,g35)
    c: PointOnObject(g34,g35)
    c: Coincident(g35,g1)
    c: PointOnObject(g34,g1)
    c: Equal(g21,g14)
    c: Equal(g21,g35)
    c: Equal(g35,g28)
    c: DistanceX(g18,g16) = 4.2
    c: Coincident(g36,g12)
    c: Vertical(g36)
    c: Coincident(g37,g9)
    c: Vertical(g37)
    c: Coincident(g38,g36)
    c: Coincident(g38,g37)
    c: Horizontal(g38)
    c: Coincident(g39,g19)
    c: Vertical(g39)
    c: Coincident(g40,g16)
    c: Vertical(g40)
    c: Coincident(g41,g39)
    c: Coincident(g41,g40)
    c: Horizontal(g41)
    c: Equal(g37,g39)
    c: Distance(g37) = 16
FEATURE [PartDesign::Pocket] Pocket020  label="I2CMtHexSunk"
  BaseFeature = -> Pocket019
  Length = 5
  Length2 = 100
  Placement = pos=(0,0,0) rot=(0.57735,0.57735,0.57735;2.0944rad)
  Profile = -> Sketch036
  Type = 1
FEATURE [Sketcher::SketchObject] Sketch037  label="Sketch_USMtCSunk"
  FullyConstrained = true
  MapMode = 5
  Placement = pos=(0,2,4e-16) rot=(1,0,0;1.5708rad)
  Support = -> [DatumPlane]
  expr: Constraints[8] = <<params>>.usr_mt_hole_height
  expr: Constraints[11] = <<params>>.usr_mt_hole_cent_loc_z
  expr: Constraints[9] = <<params>>.usr_mt_hole_width_short
  expr: Constraints[69] = <<params>>.usr_mt_hole_width_long
  expr: Constraints[72] = <<params>>.m2_nut_clear_flat
  expr: Constraints[84] = <<params>>.usr_mt_hole_width_short
  sketch-geometry (57):
    g0: LineSegment StartX=-22.625 StartY=37.25 StartZ=0 EndX=7.125 EndY=37.25 EndZ=0
    g1: LineSegment StartX=7.125 StartY=37.25 StartZ=0 EndX=7.125 EndY=16.75 EndZ=0
    g2: LineSegment StartX=7.125 StartY=16.75 StartZ=0 EndX=-22.625 EndY=16.75 EndZ=0
    g3: LineSegment StartX=-22.625 StartY=16.75 StartZ=0 EndX=-22.625 EndY=37.25 EndZ=0
    g4: GeomPoint X=7.125 Y=27 Z=0
    g5: LineSegment StartX=-22.625 StartY=29.4249 StartZ=0 EndX=-24.725 EndY=28.2124 EndZ=0
    g6: LineSegment StartX=-24.725 StartY=28.2124 StartZ=0 EndX=-24.725 EndY=25.7876 EndZ=0
    g7: LineSegment StartX=-24.725 StartY=25.7876 StartZ=0 EndX=-22.625 EndY=24.5751 EndZ=0
    g8: LineSegment StartX=-22.625 StartY=24.5751 StartZ=0 EndX=-20.525 EndY=25.7876 EndZ=0
    g9: LineSegment StartX=-20.525 StartY=25.7876 StartZ=0 EndX=-20.525 EndY=28.2124 EndZ=0
    g10: LineSegment StartX=-20.525 StartY=28.2124 StartZ=0 EndX=-22.625 EndY=29.4249 EndZ=0
    g11: Circle CenterX=-22.625 CenterY=27 CenterZ=0 NormalX=0 NormalY=0 NormalZ=1 AngleXU=0 Radius=2.42487
    g12: LineSegment StartX=4.70013 StartY=37.25 StartZ=0 EndX=5.91256 EndY=35.15 EndZ=0
    g13: LineSegment StartX=5.91256 StartY=35.15 StartZ=0 EndX=8.33744 EndY=35.15 EndZ=0
    g14: LineSegment StartX=8.33744 StartY=35.15 StartZ=0 EndX=9.54987 EndY=37.25 EndZ=0
    g15: LineSegment StartX=9.54987 StartY=37.25 StartZ=0 EndX=8.33744 EndY=39.35 EndZ=0
    g16: LineSegment StartX=8.33744 StartY=39.35 StartZ=0 EndX=5.91256 EndY=39.35 EndZ=0
    g17: LineSegment StartX=5.91256 StartY=39.35 StartZ=0 EndX=4.70013 EndY=37.25 EndZ=0
    g18: Circle CenterX=7.125 CenterY=37.25 CenterZ=0 NormalX=0 NormalY=0 NormalZ=1 AngleXU=0 Radius=2.42487
    g19: LineSegment StartX=4.70013 StartY=16.75 StartZ=0 EndX=5.91256 EndY=14.65 EndZ=0
    g20: LineSegment StartX=5.91256 StartY=14.65 StartZ=0 EndX=8.33744 EndY=14.65 EndZ=0
    g21: LineSegment StartX=8.33744 StartY=14.65 StartZ=0 EndX=9.54987 EndY=16.75 EndZ=0
    g22: LineSegment StartX=9.54987 StartY=16.75 StartZ=0 EndX=8.33744 EndY=18.85 EndZ=0
    g23: LineSegment StartX=8.33744 StartY=18.85 StartZ=0 EndX=5.91256 EndY=18.85 EndZ=0
    g24: LineSegment StartX=5.91256 StartY=18.85 StartZ=0 EndX=4.70013 EndY=16.75 EndZ=0
    g25: Circle CenterX=7.125 CenterY=16.75 CenterZ=0 NormalX=0 NormalY=0 NormalZ=1 AngleXU=0 Radius=2.42487
    g26: LineSegment StartX=-7.125 StartY=37.25 StartZ=0 EndX=22.625 EndY=37.25 EndZ=0
    g27: LineSegment StartX=22.625 StartY=37.25 StartZ=0 EndX=22.625 EndY=16.75 EndZ=0
    g28: LineSegment StartX=22.625 StartY=16.75 StartZ=0 EndX=-7.125 EndY=16.75 EndZ=0
    g29: LineSegment StartX=-7.125 StartY=16.75 StartZ=0 EndX=-7.125 EndY=37.25 EndZ=0
    g30: LineSegment StartX=-4.70013 StartY=37.25 StartZ=0 EndX=-5.91256 EndY=39.35 EndZ=0
    g31: LineSegment StartX=-5.91256 StartY=39.35 StartZ=0 EndX=-8.33744 EndY=39.35 EndZ=0
    g32: LineSegment StartX=-8.33744 StartY=39.35 StartZ=0 EndX=-9.54987 EndY=37.25 EndZ=0
    g33: LineSegment StartX=-9.54987 StartY=37.25 StartZ=0 EndX=-8.33744 EndY=35.15 EndZ=0
    g34: LineSegment StartX=-8.33744 StartY=35.15 StartZ=0 EndX=-5.91256 EndY=35.15 EndZ=0
    g35: LineSegment StartX=-5.91256 StartY=35.15 StartZ=0 EndX=-4.70013 EndY=37.25 EndZ=0
    g36: Circle CenterX=-7.125 CenterY=37.25 CenterZ=0 NormalX=0 NormalY=0 NormalZ=1 AngleXU=0 Radius=2.42487
    g37: LineSegment StartX=-9.54987 StartY=16.75 StartZ=0 EndX=-8.33744 EndY=14.65 EndZ=0
    g38: LineSegment StartX=-8.33744 StartY=14.65 StartZ=0 EndX=-5.91256 EndY=14.65 EndZ=0
    g39: LineSegment StartX=-5.91256 StartY=14.65 StartZ=0 EndX=-4.70013 EndY=16.75 EndZ=0
    g40: LineSegment StartX=-4.70013 StartY=16.75 StartZ=0 EndX=-5.91256 EndY=18.85 EndZ=0
    g41: LineSegment StartX=-5.91256 StartY=18.85 StartZ=0 EndX=-8.33744 EndY=18.85 EndZ=0
    g42: LineSegment StartX=-8.33744 StartY=18.85 StartZ=0 EndX=-9.54987 EndY=16.75 EndZ=0
    g43: Circle CenterX=-7.125 CenterY=16.75 CenterZ=0 NormalX=0 NormalY=0 NormalZ=1 AngleXU=0 Radius=2.42487
    g44: LineSegment StartX=22.625 StartY=29.4249 StartZ=0 EndX=20.525 EndY=28.2124 EndZ=0
    g45: LineSegment StartX=20.525 StartY=28.2124 StartZ=0 EndX=20.525 EndY=25.7876 EndZ=0
    g46: LineSegment StartX=20.525 StartY=25.7876 StartZ=0 EndX=22.625 EndY=24.5751 EndZ=0
    g47: LineSegment StartX=22.625 StartY=24.5751 StartZ=0 EndX=24.725 EndY=25.7876 EndZ=0
    g48: LineSegment StartX=24.725 StartY=25.7876 StartZ=0 EndX=24.725 EndY=28.2124 EndZ=0
    g49: LineSegment StartX=24.725 StartY=28.2124 StartZ=0 EndX=22.625 EndY=29.4249 EndZ=0
    g50: Circle CenterX=22.625 CenterY=27 CenterZ=0 NormalX=0 NormalY=0 NormalZ=1 AngleXU=0 Radius=2.42487
    g51: LineSegment StartX=20.525 StartY=25.7876 StartZ=0 EndX=20.525 EndY=24.5751 EndZ=0
    g52: LineSegment StartX=24.725 StartY=25.7876 StartZ=0 EndX=24.725 EndY=24.5751 EndZ=0
    g53: LineSegment StartX=20.525 StartY=24.5751 StartZ=0 EndX=24.725 EndY=24.5751 EndZ=0
    g54: LineSegment StartX=-24.725 StartY=25.7876 StartZ=0 EndX=-24.725 EndY=24.5751 EndZ=0
    g55: LineSegment StartX=-20.525 StartY=25.7876 StartZ=0 EndX=-20.525 EndY=24.5751 EndZ=0
    g56: LineSegment StartX=-20.525 StartY=24.5751 StartZ=0 EndX=-24.725 EndY=24.5751 EndZ=0
  constraints (137):
    c: Coincident(g0,g1)
    c: Coincident(g1,g2)
    c: Coincident(g2,g3)
    c: Coincident(g3,g0)
    c: Horizontal(g0)
    c: Horizontal(g2)
    c: Vertical(g1)
    c: Vertical(g3)
    c: DistanceY(g1,g0) = 20.5
    c: DistanceX(g-1,g1) = 7.125
    c: Symmetric(g1,g0,g4)
    c: DistanceY(g-1,g4) = 27
    c: Coincident(g5,g6)
    c: Coincident(g6,g7)
    c: Coincident(g7,g8)
    c: Coincident(g8,g9)
    c: Coincident(g9,g10)
    c: Coincident(g10,g5)
    c: Equal(g5, g6-g10) x5
    c: PointOnObject(g5,g11)
    c: PointOnObject(g6,g11)
    c: PointOnObject(g7,g11)
    c: PointOnObject(g8,g11)
    c: PointOnObject(g9,g11)
    c: PointOnObject(g10,g11)
    c: Coincident(g12,g13)
    c: Coincident(g13,g14)
    c: Coincident(g14,g15)
    c: Coincident(g15,g16)
    c: Coincident(g16,g17)
    c: Coincident(g17,g12)
    c: Equal(g12, g13-g17) x5
    c: PointOnObject(g12,g18)
    c: PointOnObject(g13,g18)
    c: PointOnObject(g14,g18)
    c: PointOnObject(g15,g18)
    c: PointOnObject(g16,g18)
    c: PointOnObject(g17,g18)
    c: Coincident(g18,g0)
    c: PointOnObject(g17,g0)
    c: Coincident(g19,g20)
    c: Coincident(g20,g21)
    c: Coincident(g21,g22)
    c: Coincident(g22,g23)
    c: Coincident(g23,g24)
    c: Coincident(g24,g19)
    c: Equal(g19, g20-g24) x5
    c: PointOnObject(g19,g25)
    c: PointOnObject(g20,g25)
    c: PointOnObject(g21,g25)
    c: PointOnObject(g22,g25)
    c: PointOnObject(g23,g25)
    c: PointOnObject(g24,g25)
    c: Coincident(g25,g1)
    c: PointOnObject(g24,g2)
    c: Vertical(g6)
    c: Symmetric(g0,g2,g11)
    c: DistanceX(g2,g-1) = 22.625
    c: Equal(g25,g18)
    c: Equal(g18,g11)
    c: DistanceY(g13,g15) = 4.2
    c: Coincident(g26,g27)
    c: Coincident(g27,g28)
    c: Coincident(g28,g29)
    c: Coincident(g29,g26)
    c: Horizontal(g26)
    c: Horizontal(g28)
    c: Vertical(g27)
    c: Vertical(g29)
    c: PointOnObject(g26,g0)
    c: PointOnObject(g28,g2)
    c: Equal(g0,g26)
    c: DistanceX(g28,g-1) = 7.125
    c: Coincident(g30,g31)
    c: Coincident(g31,g32)
    c: Coincident(g32,g33)
    c: Coincident(g33,g34)
    c: Coincident(g34,g35)
    c: Coincident(g35,g30)
    c: Equal(g30, g31-g35) x5
    c: PointOnObject(g30,g36)
    c: PointOnObject(g31,g36)
    c: PointOnObject(g32,g36)
    c: PointOnObject(g33,g36)
    c: PointOnObject(g34,g36)
    c: PointOnObject(g35,g36)
    c: Coincident(g36,g26)
    c: PointOnObject(g35,g0)
    c: Coincident(g37,g38)
    c: Coincident(g38,g39)
    c: Coincident(g39,g40)
    c: Coincident(g40,g41)
    c: Coincident(g41,g42)
    c: Coincident(g42,g37)
    c: Equal(g37, g38-g42) x5
    c: PointOnObject(g37,g43)
    c: PointOnObject(g38,g43)
    c: PointOnObject(g39,g43)
    c: PointOnObject(g40,g43)
    c: PointOnObject(g41,g43)
    c: PointOnObject(g42,g43)
    c: Coincident(g43,g28)
    c: PointOnObject(g42,g2)
    c: Coincident(g44,g45)
    c: Coincident(g45,g46)
    c: Coincident(g46,g47)
    c: Coincident(g47,g48)
    c: Coincident(g48,g49)
    c: Coincident(g49,g44)
    c: Equal(g44, g45-g49) x5
    c: PointOnObject(g44,g50)
    c: PointOnObject(g45,g50)
    c: PointOnObject(g46,g50)
    c: PointOnObject(g47,g50)
    c: PointOnObject(g48,g50)
    c: PointOnObject(g49,g50)
    c: Vertical(g45)
    c: Symmetric(g26,g27,g50)
    c: Equal(g18,g36)
    c: Equal(g18,g50)
    c: Equal(g18,g43)
    c: Coincident(g51,g45)
    c: Vertical(g51)
    c: Coincident(g52,g48)
    c: Vertical(g52)
    c: Coincident(g53,g51)
    c: Coincident(g53,g52)
    c: Horizontal(g53)
    c: Coincident(g54,g6)
    c: Vertical(g54)
    c: Coincident(g55,g9)
    c: Vertical(g55)
    c: Coincident(g56,g55)
    c: Coincident(g56,g54)
    c: Horizontal(g56)
    c: Equal(g55,g52)
    c: PointOnObject(g46,g53)
FEATURE [PartDesign::Pocket] Pocket021  label="USRMtHexSunk"
  BaseFeature = -> Pocket020
  Length = 5
  Length2 = 100
  Placement = pos=(0,0,0) rot=(0.57735,0.57735,0.57735;2.0944rad)
  Profile = -> Sketch037
  Type = 1
FEATURE [Sketcher::SketchObject] Sketch038
  FullyConstrained = true
  MapMode = 5
  Placement = pos=(0,0,0) rot=(1,0,0;1.5708rad)
  Support = -> [XZ_Plane001]
  expr: Constraints[26] = <<params>>.usr_mt_height
  expr: Constraints[27] = <<params>>.usr_mt_width
  expr: Constraints[12] = <<params>>.std_rad
  sketch-geometry (11):
    g0: LineSegment StartX=-24 StartY=41.5 StartZ=0 EndX=24 EndY=41.5 EndZ=0
    g1: LineSegment StartX=26 StartY=39.5 StartZ=0 EndX=26 EndY=0 EndZ=0
    g2: LineSegment StartX=-26 StartY=39.5 StartZ=0 EndX=-26 EndY=0 EndZ=0
    g3: ArcOfCircle CenterX=-24 CenterY=39.5 CenterZ=0 NormalX=0 NormalY=0 NormalZ=1 AngleXU=0 Radius=2 StartAngle=1.5708 EndAngle=3.14159
    g4: ArcOfCircle CenterX=24 CenterY=39.5 CenterZ=0 NormalX=0 NormalY=0 NormalZ=1 AngleXU=0 Radius=2 StartAngle=0 EndAngle=1.5708
    g5: LineSegment StartX=0 StartY=0 StartZ=0 EndX=0 EndY=41.5 EndZ=0
    g6: LineSegment StartX=26 StartY=0 StartZ=0 EndX=36 EndY=0 EndZ=0
    g7: LineSegment StartX=-26 StartY=0 StartZ=0 EndX=-36 EndY=0 EndZ=0
    g8: LineSegment StartX=-36 StartY=0 StartZ=0 EndX=-36 EndY=51.5 EndZ=0
    g9: LineSegment StartX=-36 StartY=51.5 StartZ=0 EndX=36 EndY=51.5 EndZ=0
    g10: LineSegment StartX=36 StartY=51.5 StartZ=0 EndX=36 EndY=0 EndZ=0
  constraints (30):
    c: Horizontal(g0)
    c: PointOnObject(g1,g-1)
    c: Vertical(g1)
    c: PointOnObject(g2,g-1)
    c: Vertical(g2)
    c: Tangent(g0,g3) = 1.5708
    c: Tangent(g2,g3) = -1.5708
    c: Tangent(g0,g4) = 1.5708
    c: Tangent(g1,g4) = 1.5708
    c: Coincident(g5,g-1)
    c: Vertical(g5)
    c: Equal(g4,g3)
    c: Radius(g4) = 2
    c: Symmetric(g0,g0,g5)
    c: Coincident(g6,g1)
    c: PointOnObject(g6,g-1)
    c: Coincident(g7,g2)
    c: PointOnObject(g7,g-1)
    c: Equal(g6,g7)
    c: Coincident(g8,g7)
    c: Vertical(g8)
    c: Coincident(g9,g8)
    c: Horizontal(g9)
    c: Coincident(g10,g9)
    c: Coincident(g10,g6)
    c: Vertical(g10)
    c: DistanceY(g-1,g5) = 41.5
    c: DistanceX(g2,g1) = 52
    c: DistanceY(g5,g9) = 10
    c: DistanceX(g1,g6) = 10
FEATURE [PartDesign::Pocket] Pocket022  label="RoundMtTop"
  BaseFeature = -> Pocket021
  Length = 5
  Length2 = 100
  Placement = pos=(0,0,0) rot=(0.57735,0.57735,0.57735;2.0944rad)
  Profile = -> Sketch038
  Type = 1
FEATURE [Sketcher::SketchObject] Sketch039
  FullyConstrained = true
  MapMode = 5
  Support = -> [XY_Plane001]
  expr: Constraints[23] = <<params>>.std_rad
  expr: Constraints[27] = <<params>>.usr_mt_foot_width
  expr: Constraints[28] = <<params>>.usr_mt_width
  sketch-geometry (11):
    g0: LineSegment StartX=-26 StartY=0 StartZ=0 EndX=-26 EndY=30 EndZ=0
    g1: LineSegment StartX=-24 StartY=32 StartZ=0 EndX=24 EndY=32 EndZ=0
    g2: LineSegment StartX=26 StartY=30 StartZ=0 EndX=26 EndY=0 EndZ=0
    g3: LineSegment StartX=26 StartY=0 StartZ=0 EndX=36 EndY=0 EndZ=0
    g4: LineSegment StartX=-26 StartY=0 StartZ=0 EndX=-36 EndY=0 EndZ=0
    g5: ArcOfCircle CenterX=-24 CenterY=30 CenterZ=0 NormalX=0 NormalY=0 NormalZ=1 AngleXU=0 Radius=2 StartAngle=1.5708 EndAngle=3.14159
    g6: ArcOfCircle CenterX=24 CenterY=30 CenterZ=0 NormalX=0 NormalY=0 NormalZ=1 AngleXU=0 Radius=2 StartAngle=-9e-16 EndAngle=1.5708
    g7: LineSegment StartX=0 StartY=0 StartZ=0 EndX=0 EndY=32 EndZ=0
    g8: LineSegment StartX=-36 StartY=0 StartZ=0 EndX=-36 EndY=42 EndZ=0
    g9: LineSegment StartX=-36 StartY=42 StartZ=0 EndX=36 EndY=42 EndZ=0
    g10: LineSegment StartX=36 StartY=42 StartZ=0 EndX=36 EndY=0 EndZ=0
  constraints (30):
    c: PointOnObject(g0,g-1)
    c: Vertical(g0)
    c: Horizontal(g1)
    c: PointOnObject(g2,g-1)
    c: Vertical(g2)
    c: Coincident(g3,g2)
    c: PointOnObject(g3,g-1)
    c: Coincident(g4,g0)
    c: PointOnObject(g4,g-1)
    c: Tangent(g0,g5) = 1.5708
    c: Tangent(g1,g5) = 1.5708
    c: Tangent(g1,g6) = 1.5708
    c: Tangent(g2,g6) = 1.5708
    c: Equal(g6,g5)
    c: Coincident(g7,g-1)
    c: PointOnObject(g7,g-2)
    c: Coincident(g8,g4)
    c: Vertical(g8)
    c: Coincident(g9,g8)
    c: Horizontal(g9)
    c: Coincident(g10,g9)
    c: Coincident(g10,g3)
    c: Vertical(g10)
    c: Radius(g6) = 2
    c: Symmetric(g1,g1,g7)
    c: DistanceX(g2,g3) = 10
    c: DistanceY(g7,g9) = 10
    c: DistanceY(g-1,g7) = 32
    c: DistanceX(g0,g2) = 52
    c: Equal(g3,g4)
FEATURE [PartDesign::Pocket] Pocket023  label="SculptFoot"
  BaseFeature = -> Pocket022
  Length = 5
  Length2 = 100
  Placement = pos=(0,0,0) rot=(0.57735,0.57735,0.57735;2.0944rad)
  Profile = -> Sketch039
  Reversed = true
  Type = 1
FEATURE [Sketcher::SketchObject] Sketch040
  FullyConstrained = true
  MapMode = 5
  Support = -> [XY_Plane029]
  expr: Constraints[10] = <<I2CExpParams>>.exp_i2c_width
  expr: Constraints[9] = <<I2CExpParams>>.exp_i2c_leng
  sketch-geometry (4):
    g0: LineSegment StartX=-15.24 StartY=8.89 StartZ=0 EndX=15.24 EndY=8.89 EndZ=0
    g1: LineSegment StartX=15.24 StartY=8.89 StartZ=0 EndX=15.24 EndY=-8.89 EndZ=0
    g2: LineSegment StartX=15.24 StartY=-8.89 StartZ=0 EndX=-15.24 EndY=-8.89 EndZ=0
    g3: LineSegment StartX=-15.24 StartY=-8.89 StartZ=0 EndX=-15.24 EndY=8.89 EndZ=0
  constraints (11):
    c: Coincident(g0,g1)
    c: Coincident(g1,g2)
    c: Coincident(g2,g3)
    c: Coincident(g3,g0)
    c: Horizontal(g0)
    c: Horizontal(g2)
    c: Vertical(g1)
    c: Vertical(g3)
    c: Symmetric(g2,g0,g-1)
    c: DistanceX(g0,g0) = 30.48
    c: DistanceY(g1,g1) = 17.78
FEATURE [PartDesign::Pad] Pad015
  Direction = (1,1,1)
  Length = 1.65
  Length2 = 100
  Profile = -> Sketch040
  Reversed = true
  Type = 0
  expr: Length = <<I2CExpParams>>.board_thickness
FEATURE [Sketcher::SketchObject] Sketch041
  FullyConstrained = true
  MapMode = 5
  Support = -> [XY_Plane024]
  sketch-geometry (4):
    g0: LineSegment StartX=-7 StartY=3.6 StartZ=0 EndX=7 EndY=3.6 EndZ=0
    g1: LineSegment StartX=7 StartY=3.6 StartZ=0 EndX=7 EndY=-3.6 EndZ=0
    g2: LineSegment StartX=7 StartY=-3.6 StartZ=0 EndX=-7 EndY=-3.6 EndZ=0
    g3: LineSegment StartX=-7 StartY=-3.6 StartZ=0 EndX=-7 EndY=3.6 EndZ=0
  constraints (11):
    c: Coincident(g0,g1)
    c: Coincident(g1,g2)
    c: Coincident(g2,g3)
    c: Coincident(g3,g0)
    c: Horizontal(g0)
    c: Horizontal(g2)
    c: Vertical(g1)
    c: Vertical(g3)
    c: DistanceX(g0,g0) = 14
    c: DistanceY(g1,g1) = 7.2
    c: Symmetric(g0,g1,g-1)
FEATURE [PartDesign::Pad] Pad016
  Direction = (1,1,1)
  Length = 1
  Length2 = 100
  Profile = -> Sketch041
  Type = 0
FEATURE [PartDesign::Body] Body023  label="Chip"
  Group = -> [Sketch041,Pad016]
  Origin = -> Origin026
  Tip = -> Pad016
FEATURE [Sketcher::SketchObject] Sketch042
  FullyConstrained = true
  MapMode = 5
  Support = -> [XY_Plane029]
  expr: Constraints[4] = <<I2CExpParams>>.exp_i2c_hole_leng_space
  expr: Constraints[3] = <<I2CExpParams>>.exp_i2c_hole_mt_diam
  sketch-geometry (2):
    g0: Circle CenterX=-12.7 CenterY=0 CenterZ=0 NormalX=0 NormalY=0 NormalZ=1 AngleXU=0 Radius=1.27
    g1: Circle CenterX=12.7 CenterY=0 CenterZ=0 NormalX=0 NormalY=0 NormalZ=1 AngleXU=0 Radius=1.27
  constraints (5):
    c: PointOnObject(g0,g-1)
    c: Symmetric(g0,g1,g-1)
    c: Equal(g0,g1)
    c: Diameter(g1) = 2.54
    c: DistanceX(g0,g1) = 25.4
FEATURE [Sketcher::SketchObject] Sketch043
  FullyConstrained = true
  MapMode = 5
  Support = -> [XY_Plane027]
  expr: Constraints[10] = <<I2CExpParams>>.exp_i2c_num_pins * <<I2CExpParams>>.pin_spacing
  expr: Constraints[9] = <<I2CExpParams>>.pin_spacing
  sketch-geometry (4):
    g0: LineSegment StartX=-15.24 StartY=1.27 StartZ=0 EndX=15.24 EndY=1.27 EndZ=0
    g1: LineSegment StartX=15.24 StartY=1.27 StartZ=0 EndX=15.24 EndY=-1.27 EndZ=0
    g2: LineSegment StartX=15.24 StartY=-1.27 StartZ=0 EndX=-15.24 EndY=-1.27 EndZ=0
    g3: LineSegment StartX=-15.24 StartY=-1.27 StartZ=0 EndX=-15.24 EndY=1.27 EndZ=0
  constraints (11):
    c: Coincident(g0,g1)
    c: Coincident(g1,g2)
    c: Coincident(g2,g3)
    c: Coincident(g3,g0)
    c: Horizontal(g0)
    c: Horizontal(g2)
    c: Vertical(g1)
    c: Vertical(g3)
    c: Symmetric(g2,g0,g-1)
    c: DistanceY(g1,g1) = 2.54
    c: DistanceX(g0,g0) = 30.48
FEATURE [PartDesign::Pad] Pad017
  Direction = (1,1,1)
  Length = 2.54
  Length2 = 100
  Profile = -> Sketch043
  Type = 0
  expr: Length = <<I2CExpParams>>.pin_square_block_dim
FEATURE [PartDesign::Body] Body024  label="PinBlock"
  Group = -> [Sketch043,Pad017]
  Origin = -> Origin031
  Placement = pos=(0,8,0) rot=(0,0,1;0rad)
  Tip = -> Pad017
FEATURE [PartDesign::FeatureBase] Clone011
  BaseFeature = -> Body024
FEATURE [PartDesign::Body] Body021  label="PinBlock001"
  BaseFeature = -> Body024
  Group = -> [Clone011]
  Origin = -> Origin025
  Placement = pos=(0,-8,0) rot=(0,0,1;0rad)
  Tip = -> Clone011
FEATURE [Sketcher::SketchObject] Sketch044
  FullyConstrained = true
  MapMode = 5
  Support = -> [XY_Plane029]
  expr: Constraints[4] = <<I2CExpParams>>.exp_i2c_pin_width_space
  expr: Constraints[3] = <<I2CExpParams>>.pin_hole_diam
  sketch-geometry (2):
    g0: Circle CenterX=0 CenterY=-7.62 CenterZ=0 NormalX=0 NormalY=0 NormalZ=1 AngleXU=0 Radius=0.4
    g1: Circle CenterX=0 CenterY=7.62 CenterZ=0 NormalX=0 NormalY=0 NormalZ=1 AngleXU=0 Radius=0.4
  constraints (5):
    c: PointOnObject(g0,g-2)
    c: Equal(g1,g0)
    c: Symmetric(g1,g0,g-1)
    c: Diameter(g1) = 0.8
    c: DistanceY(g0,g1) = 15.24
FEATURE [Sketcher::SketchObject] Sketch045
  FullyConstrained = true
  MapMode = 5
  Placement = pos=(0,0,0) rot=(1,0,0;1.5708rad)
  Support = -> [XZ_Plane032]
  expr: Constraints[12] = <<I2CExpParams>>.pin_square_block_dim
  expr: Constraints[11] = <<I2CExpParams>>.pin_jumper_leng
  expr: Constraints[10] = <<I2CExpParams>>.exp_i2c_leng
  sketch-geometry (5):
    g0: LineSegment StartX=-15.24 StartY=16.64 StartZ=0 EndX=15.24 EndY=16.64 EndZ=0
    g1: LineSegment StartX=15.24 StartY=16.64 StartZ=0 EndX=15.24 EndY=2.54 EndZ=0
    g2: LineSegment StartX=15.24 StartY=2.54 StartZ=0 EndX=-15.24 EndY=2.54 EndZ=0
    g3: LineSegment StartX=-15.24 StartY=2.54 StartZ=0 EndX=-15.24 EndY=16.64 EndZ=0
    g4: GeomPoint X=0 Y=2.54 Z=0
  constraints (13):
    c: Coincident(g0,g1)
    c: Coincident(g1,g2)
    c: Coincident(g2,g3)
    c: Coincident(g3,g0)
    c: Horizontal(g0)
    c: Horizontal(g2)
    c: Vertical(g1)
    c: Vertical(g3)
    c: PointOnObject(g4,g-2)
    c: Symmetric(g2,g1,g4)
    c: DistanceX(g0,g0) = 30.48
    c: DistanceY(g1,g1) = 14.1
    c: DistanceY(g-1,g4) = 2.54
FEATURE [PartDesign::Pad] Pad004
  Direction = (1,1,1)
  Length = 2.54
  Length2 = 100
  Midplane = true
  Placement = pos=(0,0,0) rot=(1,0,0;1.5708rad)
  Profile = -> Sketch045
  Type = 0
  expr: Length = <<I2CExpParams>>.pin_square_block_dim
FEATURE [PartDesign::Body] Body026  label="JumperHeader"
  Group = -> [Sketch045,Pad004]
  Origin = -> Origin024
  Placement = pos=(0,8,0) rot=(0,0,1;0rad)
  Tip = -> Pad004
FEATURE [PartDesign::FeatureBase] Clone012
  BaseFeature = -> Body026
FEATURE [PartDesign::Body] Body020  label="JumperHeader001"
  BaseFeature = -> Body026
  Group = -> [Clone012]
  Origin = -> Origin032
  Placement = pos=(0,-8,0) rot=(0,0,1;0rad)
  Tip = -> Clone012
FEATURE [Sketcher::SketchObject] Sketch007
  FullyConstrained = true
  MapMode = 5
  Placement = pos=(0,0,0) rot=(1,0,0;1.5708rad)
  Support = -> [XZ_Plane026]
  expr: Constraints[27] = <<I2CExpParams>>.pin_spacing
  expr: Constraints[28] = <<I2CExpParams>>.pin_leng * 2
  expr: Constraints[21] = <<I2CExpParams>>.pin_width
  expr: Constraints[20] = <<I2CExpParams>>.pin_square_block_dim - <<I2CExpParams>>.std_tol
  sketch-geometry (13):
    g0: LineSegment StartX=-2.24 StartY=14.64 StartZ=0 EndX=-0.3 EndY=14.64 EndZ=0
    g1: LineSegment StartX=-0.3 StartY=14.64 StartZ=0 EndX=-0.3 EndY=2.24 EndZ=0
    g2: LineSegment StartX=-0.3 StartY=2.24 StartZ=0 EndX=-2.24 EndY=2.24 EndZ=0
    g3: LineSegment StartX=-2.24 StartY=2.24 StartZ=0 EndX=-2.24 EndY=14.64 EndZ=0
    g4: LineSegment StartX=0.3 StartY=14.64 StartZ=0 EndX=2.24 EndY=14.64 EndZ=0
    g5: LineSegment StartX=2.24 StartY=14.64 StartZ=0 EndX=2.24 EndY=2.24 EndZ=0
    g6: LineSegment StartX=2.24 StartY=2.24 StartZ=0 EndX=0.3 EndY=2.24 EndZ=0
    g7: LineSegment StartX=0.3 StartY=2.24 StartZ=0 EndX=0.3 EndY=14.64 EndZ=0
    g8: LineSegment StartX=-0.3 StartY=14.64 StartZ=0 EndX=0.3 EndY=14.64 EndZ=0
    g9: LineSegment StartX=-0.3 StartY=2.24 StartZ=0 EndX=0.3 EndY=2.24 EndZ=0
    g10: GeomPoint X=0 Y=2.24 Z=0
    g11: GeomPoint X=-1.27 Y=2.24 Z=0
    g12: GeomPoint X=1.27 Y=2.24 Z=0
  constraints (30):
    c: Coincident(g0,g1)
    c: Coincident(g1,g2)
    c: Coincident(g2,g3)
    c: Coincident(g3,g0)
    c: Horizontal(g0)
    c: Horizontal(g2)
    c: Vertical(g1)
    c: Vertical(g3)
    c: Coincident(g4,g5)
    c: Coincident(g5,g6)
    c: Coincident(g6,g7)
    c: Coincident(g7,g4)
    c: Horizontal(g4)
    c: Vertical(g5)
    c: Vertical(g7)
    c: Coincident(g8,g0)
    c: Coincident(g8,g4)
    c: Coincident(g9,g1)
    c: Coincident(g9,g6)
    c: Horizontal(g8)
    c: DistanceY(g-1,g5) = 2.24
    c: DistanceX(g8,g8) = 0.6
    c: PointOnObject(g10,g-2)
    c: Symmetric(g1,g6,g10)
    c: Symmetric(g2,g1,g11)
    c: Symmetric(g6,g5,g12)
    c: Symmetric(g11,g12,g10)
    c: DistanceX(g11,g12) = 2.54
    c: DistanceY(g5,g5) = 12.4
    c: Horizontal(g9)
FEATURE [Sketcher::SketchObject] Sketch006
  FullyConstrained = true
  MapMode = 5
  Placement = pos=(0,0,0) rot=(1,0,0;1.5708rad)
  Support = -> [XZ_Plane028]
  expr: Constraints[9] = <<I2CExpParams>>.pin_square_block_dim + <<I2CExpParams>>.pin_leng
  expr: Constraints[10] = <<I2CExpParams>>.exp_i2c_leng
  sketch-geometry (4):
    g0: LineSegment StartX=-15.24 StartY=8.74 StartZ=0 EndX=15.24 EndY=8.74 EndZ=0
    g1: LineSegment StartX=15.24 StartY=8.74 StartZ=0 EndX=15.24 EndY=0 EndZ=0
    g2: LineSegment StartX=15.24 StartY=0 StartZ=0 EndX=-15.24 EndY=0 EndZ=0
    g3: LineSegment StartX=-15.24 StartY=0 StartZ=0 EndX=-15.24 EndY=8.74 EndZ=0
  constraints (11):
    c: Coincident(g0,g1)
    c: Coincident(g1,g2)
    c: Coincident(g2,g3)
    c: Coincident(g3,g0)
    c: Horizontal(g0)
    c: Horizontal(g2)
    c: Vertical(g1)
    c: Vertical(g3)
    c: Symmetric(g2,g1,g-1)
    c: DistanceY(g1,g1) = 8.74
    c: DistanceX(g2,g2) = 30.48
FEATURE [PartDesign::Pad] Pad014
  Direction = (1,1,1)
  Length = 0.6
  Length2 = 100
  Midplane = true
  Placement = pos=(0,0,0) rot=(1,0,0;1.5708rad)
  Profile = -> Sketch006
  Type = 0
  expr: Length = <<I2CExpParams>>.pin_width
FEATURE [PartDesign::Pocket] Pocket002
  BaseFeature = -> Pad014
  Length = 5
  Length2 = 100
  Midplane = true
  Placement = pos=(0,0,0) rot=(1,0,0;1.5708rad)
  Profile = -> Sketch007
  Type = 1
FEATURE [PartDesign::Pocket] Pocket024
  BaseFeature = -> Pad015
  Length = 5
  Length2 = 100
  Profile = -> Sketch042
  Type = 1
FEATURE [PartDesign::Pocket] Pocket025
  BaseFeature = -> Pocket024
  Length = 5
  Length2 = 100
  Profile = -> Sketch044
  Type = 1
FEATURE [PartDesign::LinearPattern] LinearPattern
  BaseFeature = -> Pocket025
  Direction = -> X_Axis031
  Length = 30.48
  Occurrences = 12
  Originals = -> [Pocket025]
  expr: Length = <<I2CExpParams>>.pin_spacing * <<I2CExpParams>>.exp_i2c_num_pins
  expr: Occurrences = <<I2CExpParams>>.exp_i2c_num_pins
FEATURE [PartDesign::LinearPattern] LinearPattern001
  BaseFeature = -> LinearPattern
  Direction = -> X_Axis031
  Length = 30.48
  Occurrences = 12
  Originals = -> [Pocket025]
  Reversed = true
  expr: Occurrences = <<I2CExpParams>>.exp_i2c_num_pins
  expr: Length = <<I2CExpParams>>.pin_spacing * <<I2CExpParams>>.exp_i2c_num_pins
FEATURE [PartDesign::Body] Body027  label="MainBoard"
  Group = -> [Sketch040,Pad015,Sketch042,Pocket024,Sketch044,Pocket025,LinearPattern,LinearPattern001]
  Origin = -> Origin030
  Tip = -> LinearPattern001
FEATURE [PartDesign::LinearPattern] LinearPattern002
  BaseFeature = -> Pocket002
  Direction = -> X_Axis026
  Length = 30.48
  Occurrences = 12
  Originals = -> [Pocket002]
  Placement = pos=(0,0,0) rot=(1,0,0;1.5708rad)
  expr: Occurrences = <<I2CExpParams>>.exp_i2c_num_pins
  expr: Length = <<I2CExpParams>>.pin_spacing * <<I2CExpParams>>.exp_i2c_num_pins
FEATURE [PartDesign::LinearPattern] LinearPattern003
  BaseFeature = -> LinearPattern002
  Direction = -> X_Axis026
  Length = 30.48
  Occurrences = 12
  Originals = -> [Pocket002]
  Placement = pos=(0,0,0) rot=(1,0,0;1.5708rad)
  Reversed = true
  expr: Occurrences = <<I2CExpParams>>.exp_i2c_num_pins
  expr: Length = <<I2CExpParams>>.pin_spacing * <<I2CExpParams>>.exp_i2c_num_pins
FEATURE [PartDesign::Body] Body022  label="Pins"
  Group = -> [Sketch006,Pad014,Sketch007,Pocket002,LinearPattern002,LinearPattern003]
  Origin = -> Origin027
  Placement = pos=(0,-8,0) rot=(0,0,1;0rad)
  Tip = -> LinearPattern003
FEATURE [PartDesign::FeatureBase] Clone013
  BaseFeature = -> Body022
  Placement = pos=(0,-8,0) rot=(0,0,1;0rad)
FEATURE [PartDesign::Body] Body025  label="Pins001"
  BaseFeature = -> Body022
  Group = -> [Clone013]
  Origin = -> Origin028
  Placement = pos=(0,16,0) rot=(0,0,1;0rad)
  Tip = -> Clone013
FEATURE [App::Part] Part004  label="AdaF_I2CExp_Part"
  Group = -> [Body027,Body023,Body024,Body021,Body022,Body025,Body026,Body020]
  Origin = -> Origin029
  Placement = pos=(0,8,31) rot=(1,0,0;4.71239rad)
FEATURE [Spreadsheet::Sheet] Spreadsheet001  label="I2CExpParams"
  cells = A1=Inch to mm; B1(intomm)==25.4mm; E1=std tol; F1(std_tol)==0.3mm; A3=Adafruit I2C Exp; E3=Adafruit Temp I2C; I3=Adafruit Light; B4=Inch; C4=mm; F4=Inch; G4=mm; J4=Inch; K4=mm; A5=Length; B5=1.2; C5(exp_i2c_leng)==B5 * B$1; E5=Length; F5=0.8; G5(temp_leng)==F5 * $B$1; I5=Length; J5=0.65; K5(light_leng)==J5 * $B$1; A6=Width; B6=0.7; C6(exp_i2c_width)==B6 * B$1; E6=Width; F6=0.5; G6(temp_width)==F6 * $B$1; I6=Width; J6=0.65; K6(light_width)==J6 * $B$1; A7=Hole Leng Space; B7=1; C7(exp_i2c_hole_leng_space)==B7 * B$1; E7=Hole Leng Space; F7=0.6; G7(temp_hole_leng_space)==F7 * $B$1; I7=Hole Leng Space; J7=0.45; K7(light_hole_leng_space)==J7 * $B$1; A8=Hole Diam; B8=0.1; C8(exp_i2c_hole_mt_diam)==B8 * B$1; E8=Hole Diam; F8=0.1; G8(temp_hole_diam)==F8 * $B$1; I8=Hole Diam; J8=0.1; K8(light_hole_diam)==J8 * $B$1; A9=Num Pins; B9(exp_i2c_num_pins)=12; E9=Hole Edge Offset; F9=0.1; G9(temp_hole_edge_offset)==F9 * $B$1; I9=Hole Edge Offset; J9=0.1; K9(light_hole_edge_offset)==J9 * $B$1; A10=Pin Width Space; B10=0.6; C10(exp_i2c_pin_width_space)==B10 * B$1; E10=Pin Edge Offset; F10=0.09; G10(temp_pin_edge_offset)==F10 * $B$1; I10=Pin Edge Offset; J10=0.1; K10(light_pin_edge_offset)==J10 * $B$1; E11=Num Pins; F11(temp_num_pins)=8; I11=Num Pins; J11(light_num_pins)=5; A12=General Parameters; A13=Board Thick; B13(board_thickness)==1.65mm; A15=Pin Hole Diam; B15(pin_hole_diam)==0.8mm; A16=Pin Hole Space; B16(pin_hole_space)==2.54mm; A17=Pin Width; B17(pin_width)==0.6mm; A18=Pin Square Block Dim; B18(pin_square_block_dim)==2.54mm; A19=Pin Leng; B19(pin_leng)==6.2mm; A20=Pin Jumper Leng; B20(pin_jumper_leng)==14.1mm; A21=Pin Spacing; B21(pin_spacing)==2.54mm
FEATURE [Sketcher::SketchObject] Sketch046  label="Sketch_I2CExpMtHoles"
  FullyConstrained = true
  MapMode = 5
  Placement = pos=(0,0,0) rot=(1,0,0;1.5708rad)
  Support = -> [XZ_Plane001]
  expr: Constraints[5] = <<params>>.exp_i2c_hole_space
  expr: Constraints[6] = <<params>>.exp_i2c_mt_height
  expr: Constraints[7] = <<params>>.m2_hole_clear_diam
  sketch-geometry (4):
    g0: Circle CenterX=-12.7 CenterY=31 CenterZ=0 NormalX=0 NormalY=0 NormalZ=1 AngleXU=0 Radius=1.25
    g1: Circle CenterX=12.7 CenterY=31 CenterZ=0 NormalX=0 NormalY=0 NormalZ=1 AngleXU=0 Radius=1.25
    g2: LineSegment StartX=-12.7 StartY=31 StartZ=0 EndX=12.7 EndY=31 EndZ=0
    g3: GeomPoint X=0 Y=31 Z=0
  constraints (9):
    c: Coincident(g2,g0)
    c: Coincident(g2,g1)
    c: Horizontal(g2)
    c: PointOnObject(g3,g-2)
    c: Symmetric(g0,g1,g3)
    c: DistanceX(g0,g1) = 25.4
    c: DistanceY(g-1,g3) = 31
    c: Diameter(g1) = 2.5
    c: Equal(g1,g0)
FEATURE [PartDesign::Pocket] Pocket026  label="Pocket_I2CExp_MtHoles"
  BaseFeature = -> Pocket023
  Length = 5
  Length2 = 100
  Placement = pos=(0,0,0) rot=(0.57735,0.57735,0.57735;2.0944rad)
  Profile = -> Sketch046
  Type = 1
FEATURE [Sketcher::SketchObject] Sketch047  label="Sketch_I2CExp_HexSunk"
  FullyConstrained = true
  MapMode = 5
  Placement = pos=(0,0,0) rot=(1,0,0;1.5708rad)
  Support = -> [XZ_Plane001]
  expr: Constraints[42] = <<params>>.m2_nut_clear_flat
  expr: Constraints[43] = <<params>>.exp_i2c_mt_height
  expr: Constraints[44] = <<params>>.exp_i2c_hole_space
  sketch-geometry (16):
    g0: LineSegment StartX=15.1249 StartY=31 StartZ=0 EndX=13.9124 EndY=33.1 EndZ=0
    g1: LineSegment StartX=13.9124 StartY=33.1 StartZ=0 EndX=11.4876 EndY=33.1 EndZ=0
    g2: LineSegment StartX=11.4876 StartY=33.1 StartZ=0 EndX=10.2751 EndY=31 EndZ=0
    g3: LineSegment StartX=10.2751 StartY=31 StartZ=0 EndX=11.4876 EndY=28.9 EndZ=0
    g4: LineSegment StartX=11.4876 StartY=28.9 StartZ=0 EndX=13.9124 EndY=28.9 EndZ=0
    g5: LineSegment StartX=13.9124 StartY=28.9 StartZ=0 EndX=15.1249 EndY=31 EndZ=0
    g6: Circle CenterX=12.7 CenterY=31 CenterZ=0 NormalX=0 NormalY=0 NormalZ=1 AngleXU=0 Radius=2.42487
    g7: LineSegment StartX=-10.2751 StartY=31 StartZ=0 EndX=-11.4876 EndY=33.1 EndZ=0
    g8: LineSegment StartX=-11.4876 StartY=33.1 StartZ=0 EndX=-13.9124 EndY=33.1 EndZ=0
    g9: LineSegment StartX=-13.9124 StartY=33.1 StartZ=0 EndX=-15.1249 EndY=31 EndZ=0
    g10: LineSegment StartX=-15.1249 StartY=31 StartZ=0 EndX=-13.9124 EndY=28.9 EndZ=0
    g11: LineSegment StartX=-13.9124 StartY=28.9 StartZ=0 EndX=-11.4876 EndY=28.9 EndZ=0
    g12: LineSegment StartX=-11.4876 StartY=28.9 StartZ=0 EndX=-10.2751 EndY=31 EndZ=0
    g13: Circle CenterX=-12.7 CenterY=31 CenterZ=0 NormalX=0 NormalY=0 NormalZ=1 AngleXU=0 Radius=2.42487
    g14: LineSegment StartX=-12.7 StartY=31 StartZ=0 EndX=12.7 EndY=31 EndZ=0
    g15: GeomPoint X=0 Y=31 Z=0
  constraints (37):
    c: Coincident(g0,g1)
    c: Coincident(g1,g2)
    c: Coincident(g2,g3)
    c: Coincident(g3,g4)
    c: Coincident(g4,g5)
    c: Coincident(g5,g0)
    c: Equal(g0, g1-g5) x5
    c: PointOnObject(g0,g6)
    c: PointOnObject(g1,g6)
    c: PointOnObject(g2,g6)
    c: PointOnObject(g3,g6)
    c: PointOnObject(g4,g6)
    c: PointOnObject(g5,g6)
    c: Coincident(g7,g8)
    c: Coincident(g8,g9)
    c: Coincident(g9,g10)
    c: Coincident(g10,g11)
    c: Coincident(g11,g12)
    c: Coincident(g12,g7)
    c: Equal(g7, g8-g12) x5
    c: PointOnObject(g7,g13)
    c: PointOnObject(g8,g13)
    c: PointOnObject(g9,g13)
    c: PointOnObject(g10,g13)
    c: PointOnObject(g11,g13)
    c: PointOnObject(g12,g13)
    c: Coincident(g14,g13)
    c: Coincident(g14,g6)
    c: Horizontal(g14)
    c: Equal(g13,g6)
    c: Horizontal(g8)
    c: Horizontal(g1)
    c: PointOnObject(g15,g-2)
    c: Symmetric(g13,g6,g15)
    c: DistanceY(g4,g1) = 4.2
    c: DistanceY(g-1,g15) = 31
    c: DistanceX(g13,g6) = 25.4
FEATURE [PartDesign::Pocket] Pocket027  label="Pocket_I2CExp_HexSunk"
  BaseFeature = -> Pocket026
  Length = 2.3
  Length2 = 100
  Placement = pos=(0,0,0) rot=(0.57735,0.57735,0.57735;2.0944rad)
  Profile = -> Sketch047
  Type = 0
  expr: Length = <<params>>.m2_nut_min_depth + <<params>>.std_tol_clear
FEATURE [Sketcher::SketchObject] Sketch064
  FullyConstrained = true
  MapMode = 5
  Placement = pos=(0,0,0) rot=(0.57735,0.57735,0.57735;2.0944rad)
  Support = -> [YZ_Plane001]
  expr: Constraints[3] = <<params>>.usr_mt_foot_width
  expr: Constraints[9] = <<params>>.usr_mt_side_arch_width
  expr: Constraints[18] = <<params>>.usr_mt_side_arch_vert_height
  expr: Constraints[19] = <<params>>.i2c_mt_plate_height - <<params>>.i2c_mt_plate_thick
  expr: Constraints[20] = Spreadsheet.usr_mt_side_arch_offset
  sketch-geometry (8):
    g0: LineSegment StartX=0 StartY=0 StartZ=0 EndX=32 EndY=0 EndZ=0
    g1: GeomPoint X=16 Y=0 Z=0
    g2: LineSegment StartX=10 StartY=0 StartZ=0 EndX=24 EndY=0 EndZ=0
    g3: LineSegment StartX=11.6782 StartY=8 StartZ=0 EndX=17.2872 EndY=8 EndZ=0
    g4: LineSegment StartX=17.2872 StartY=8 StartZ=0 EndX=24 EndY=0 EndZ=0
    g5: LineSegment StartX=10 StartY=0 StartZ=0 EndX=10 EndY=6 EndZ=0
    g6: LineSegment StartX=10 StartY=6 StartZ=0 EndX=11.6782 EndY=8 EndZ=0
    g7: LineSegment StartX=10 StartY=6 StartZ=0 EndX=18.9654 EndY=6 EndZ=0
  constraints (22):
    c: Coincident(g0,g-1)
    c: PointOnObject(g0,g-1)
    c: Symmetric(g0,g-1,g1)
    c: DistanceX(g0,g0) = 32
    c: Horizontal(g2)
    c: Horizontal(g3)
    c: Coincident(g4,g3)
    c: Coincident(g4,g2)
    c: Angle(g4,g2) = 0.872665
    c: DistanceX(g2,g2) = 14
    c: Coincident(g5,g2)
    c: Vertical(g5)
    c: Coincident(g6,g5)
    c: Coincident(g6,g3)
    c: Coincident(g7,g5)
    c: PointOnObject(g7,g4)
    c: Horizontal(g7)
    c: Angle(g7,g6) = 0.872665
    c: DistanceY(g5,g5) = 6
    c: DistanceY(g2,g3) = 8
    c: DistanceX(g1,g2) = 8
    c: PointOnObject(g2,g0)
FEATURE [PartDesign::Pocket] Pocket034  label="Pocket_SideArch"
  BaseFeature = -> Pocket027
  Length = 5
  Length2 = 100
  Midplane = true
  Placement = pos=(0,0,0) rot=(0.57735,0.57735,0.57735;2.0944rad)
  Profile = -> Sketch064
  Type = 1
FEATURE [PartDesign::Plane] DatumPlane006  label="Datum_LightSensMt"
  AttachmentOffset = pos=(0,0,-2.8) rot=(0,0,1;0rad)
  Length = 63.761
  MapMode = 5
  Placement = pos=(0,2.8,6e-16) rot=(1,0,0;1.5708rad)
  ResizeMode = 0
  Support = -> [XZ_Plane001]
  Width = 78.261
  expr: .AttachmentOffset.Base.z = -1 * <<params>>.usr_mt_vert_thick_top + <<params>>.lightmt_thick_cent
FEATURE [Sketcher::SketchObject] Sketch065
  FullyConstrained = true
  MapMode = 5
  Placement = pos=(0,2.8,6e-16) rot=(1,0,0;1.5708rad)
  Support = -> [DatumPlane006]
  expr: Constraints[10] = <<params>>.usr_mt_width + <<params>>.std_tol_clear
  expr: Constraints[11] = <<params>>.lightmt_height + <<params>>.std_tol_clear
  expr: Constraints[12] = <<params>>.lightsens_loc_z + <<params>>.lightmt_height / 2
  sketch-geometry (5):
    g0: LineSegment StartX=-26.15 StartY=24.65 StartZ=0 EndX=26.15 EndY=24.65 EndZ=0
    g1: LineSegment StartX=26.15 StartY=24.65 StartZ=0 EndX=26.15 EndY=16.35 EndZ=0
    g2: LineSegment StartX=26.15 StartY=16.35 StartZ=0 EndX=-26.15 EndY=16.35 EndZ=0
    g3: LineSegment StartX=-26.15 StartY=16.35 StartZ=0 EndX=-26.15 EndY=24.65 EndZ=0
    g4: GeomPoint X=0 Y=20.5 Z=0
  constraints (13):
    c: Coincident(g0,g1)
    c: Coincident(g1,g2)
    c: Coincident(g2,g3)
    c: Coincident(g3,g0)
    c: Horizontal(g0)
    c: Horizontal(g2)
    c: Vertical(g1)
    c: Vertical(g3)
    c: PointOnObject(g4,g-2)
    c: Symmetric(g2,g0,g4)
    c: DistanceX(g0,g0) = 52.3
    c: DistanceY(g1,g1) = 8.3
    c: DistanceY(g-1,g4) = 20.5
FEATURE [PartDesign::Pocket] Pocket035  label="Pocket_Slot_LightSensMt"
  BaseFeature = -> Pocket034
  Length = 5
  Length2 = 100
  Placement = pos=(0,0,0) rot=(0.57735,0.57735,0.57735;2.0944rad)
  Profile = -> Sketch065
  Type = 1
FEATURE [Sketcher::SketchObject] Sketch066  label="Sketch_HolesLightSens"
  FullyConstrained = true
  MapMode = 5
  Placement = pos=(0,0,0) rot=(1,0,0;1.5708rad)
  Support = -> [XZ_Plane001]
  expr: Constraints[6] = <<params>>.lightsens_loc_z + <<params>>.lightmt_height / 2
  expr: Constraints[7] = <<params>>.lightmt_hole_space_leng
  expr: Constraints[8] = <<params>>.m2_hole_clear_diam
  sketch-geometry (4):
    g0: LineSegment StartX=-20 StartY=20.5 StartZ=0 EndX=20 EndY=20.5 EndZ=0
    g1: GeomPoint X=0 Y=20.5 Z=0
    g2: Circle CenterX=-20 CenterY=20.5 CenterZ=0 NormalX=0 NormalY=0 NormalZ=1 AngleXU=0 Radius=1.25
    g3: Circle CenterX=20 CenterY=20.5 CenterZ=0 NormalX=0 NormalY=0 NormalZ=1 AngleXU=0 Radius=1.25
  constraints (9):
    c: Horizontal(g0)
    c: PointOnObject(g1,g-2)
    c: Symmetric(g0,g0,g1)
    c: Coincident(g2,g0)
    c: Coincident(g3,g0)
    c: Equal(g2,g3)
    c: DistanceY(g-1,g1) = 20.5
    c: DistanceX(g0,g0) = 40
    c: Diameter(g3) = 2.5
FEATURE [PartDesign::Pocket] Pocket036  label="Pocket_Holes_LightSensMt"
  BaseFeature = -> Pocket035
  Length = 5
  Length2 = 100
  Placement = pos=(0,0,0) rot=(0.57735,0.57735,0.57735;2.0944rad)
  Profile = -> Sketch066
  Type = 1
FEATURE [Sketcher::SketchObject] Sketch067  label="Sketch_CSunkLightSens"
  FullyConstrained = true
  MapMode = 5
  Placement = pos=(0,0,0) rot=(1,0,0;1.5708rad)
  Support = -> [XZ_Plane001]
  expr: Constraints[8] = <<params>>.m2_head_clear_diam
  expr: Constraints[7] = <<params>>.lightmt_hole_space_leng
  expr: Constraints[6] = <<params>>.lightsens_loc_z + <<params>>.lightmt_height / 2
  sketch-geometry (4):
    g0: LineSegment StartX=-20 StartY=20.5 StartZ=0 EndX=20 EndY=20.5 EndZ=0
    g1: GeomPoint X=0 Y=20.5 Z=0
    g2: Circle CenterX=-20 CenterY=20.5 CenterZ=0 NormalX=0 NormalY=0 NormalZ=1 AngleXU=0 Radius=2.1
    g3: Circle CenterX=20 CenterY=20.5 CenterZ=0 NormalX=0 NormalY=0 NormalZ=1 AngleXU=0 Radius=2.1
  constraints (9):
    c: Horizontal(g0)
    c: PointOnObject(g1,g-2)
    c: Symmetric(g0,g0,g1)
    c: Coincident(g2,g0)
    c: Coincident(g3,g0)
    c: Equal(g2,g3)
    c: DistanceY(g-1,g1) = 20.5
    c: DistanceX(g0,g0) = 40
    c: Diameter(g3) = 4.2
FEATURE [PartDesign::Pocket] Pocket037  label="Pocket_CSunk_LightSens"
  BaseFeature = -> Pocket036
  Length = 2
  Length2 = 100
  Placement = pos=(0,0,0) rot=(0.57735,0.57735,0.57735;2.0944rad)
  Profile = -> Sketch067
  Type = 0
  expr: Length = <<params>>.m2_head_min_depth
FEATURE [PartDesign::Body] Body  label="PB3D_USMount"
  Group = -> [Sketch016,Pad009,Sketch025,Pocket011,Sketch026,Pocket012,DatumPlane,DatumPlane001,DatumPlane002,DatumPlane003,DatumPlane004,DatumPlane005,Sketch027,Sketch030,Sketch031,Pocket015,Sketch032,Pocket016,Sketch033,Pocket017,Sketch034,Pocket018,Sketch035,Pocket019,Sketch036,Pocket020,Sketch037,Pocket021,Sketch038,Pocket022,Sketch039,Pocket023,Sketch046,Pocket026,Sketch047,Pocket027,Sketch064,Pocket034,+7 more]
  Origin = -> Origin001
  Tip = -> Pocket037
FEATURE [Spreadsheet::Sheet] Spreadsheet002  label="shield_params"
  cells = A1=Thick; B1(thick)==0.6mm; A3=I2C Exp Shield; C3=USR Shield; A4=Leng; B4(exp_leng)==32mm; C4=Leng; D4(usr_leng)==52mm; A5=Width; B5(exp_width)==20mm; C5=Width; D5(usr_width)==28mm; A6=Hole Space; B6(exp_hole_space)==25.4mm; C6=Rad; D6(usr_rad)==2mm; A7=Hole Diam; B7(exp_hole_diam)==2.54mm; A8=Thick; B8(exp_thick)==1.6mm
FEATURE [Sketcher::SketchObject] Sketch068
  FullyConstrained = true
  MapMode = 5
  Placement = pos=(0,0,0) rot=(1,0,0;1.5708rad)
  Support = -> [XZ_Plane033]
  expr: Constraints[17] = <<shield_params>>.usr_rad
  expr: Constraints[18] = <<shield_params>>.usr_leng
  expr: Constraints[19] = <<shield_params>>.usr_width
  expr: Constraints[20] = <<params>>.usr_mt_hole_cent_loc_z
  sketch-geometry (9):
    g0: LineSegment StartX=-24 StartY=41 StartZ=0 EndX=24 EndY=41 EndZ=0
    g1: LineSegment StartX=26 StartY=39 StartZ=0 EndX=26 EndY=15 EndZ=0
    g2: LineSegment StartX=24 StartY=13 StartZ=0 EndX=-24 EndY=13 EndZ=0
    g3: LineSegment StartX=-26 StartY=15 StartZ=0 EndX=-26 EndY=39 EndZ=0
    g4: ArcOfCircle CenterX=-24 CenterY=39 CenterZ=0 NormalX=0 NormalY=0 NormalZ=1 AngleXU=0 Radius=2 StartAngle=1.5708 EndAngle=3.14159
    g5: ArcOfCircle CenterX=24 CenterY=39 CenterZ=0 NormalX=0 NormalY=0 NormalZ=1 AngleXU=0 Radius=2 StartAngle=1.5e-15 EndAngle=1.5708
    g6: ArcOfCircle CenterX=24 CenterY=15 CenterZ=0 NormalX=0 NormalY=0 NormalZ=1 AngleXU=0 Radius=2 StartAngle=4.71239 EndAngle=6.28319
    g7: ArcOfCircle CenterX=-24 CenterY=15 CenterZ=0 NormalX=0 NormalY=0 NormalZ=1 AngleXU=0 Radius=2 StartAngle=3.14159 EndAngle=4.71239
    g8: GeomPoint X=0 Y=27 Z=0
  constraints (21):
    c: Horizontal(g0)
    c: Horizontal(g2)
    c: Vertical(g1)
    c: Vertical(g3)
    c: Tangent(g3,g4) = 1.5708
    c: Tangent(g0,g4) = 1.5708
    c: Tangent(g0,g5) = 1.5708
    c: Tangent(g1,g5) = 1.5708
    c: Tangent(g1,g6) = 1.5708
    c: Tangent(g2,g6) = 1.5708
    c: Tangent(g2,g7) = 1.5708
    c: Tangent(g3,g7) = 1.5708
    c: Equal(g4,g5)
    c: Equal(g6,g5)
    c: Equal(g6,g7)
    c: PointOnObject(g8,g-2)
    c: Symmetric(g7,g5,g8)
    c: Radius(g5) = 2
    c: DistanceX(g3,g1) = 52
    c: DistanceY(g2,g0) = 28
    c: DistanceY(g-1,g8) = 27
FEATURE [PartDesign::Pad] Pad018  label="Pad_MainPlate"
  Direction = (1,1,1)
  Length = 0.6
  Length2 = 100
  Placement = pos=(0,0,0) rot=(1,0,0;1.5708rad)
  Profile = -> Sketch068
  Type = 0
  expr: Length = <<shield_params>>.thick
FEATURE [Sketcher::SketchObject] Sketch069  label="Sketch_USMtHoles001"
  FullyConstrained = true
  MapMode = 5
  Placement = pos=(0,0,0) rot=(1,0,0;1.5708rad)
  Support = -> [XZ_Plane033]
  expr: Constraints[30] = <<params>>.usr_mt_hole_width_short
  expr: Constraints[18] = <<params>>.usr_mt_hole_width_long
  expr: Constraints[8] = <<params>>.usr_mt_hole_height
  expr: Constraints[16] = <<params>>.usr_mt_hole_cent_loc_z
  expr: Constraints[9] = <<params>>.usr_mt_hole_width_short
  expr: Constraints[17] = <<params>>.m2_hole_clear_diam
  sketch-geometry (15):
    g0: LineSegment StartX=-22.625 StartY=37.25 StartZ=0 EndX=7.125 EndY=37.25 EndZ=0
    g1: LineSegment StartX=7.125 StartY=37.25 StartZ=0 EndX=7.125 EndY=16.75 EndZ=0
    g2: LineSegment StartX=7.125 StartY=16.75 StartZ=0 EndX=-22.625 EndY=16.75 EndZ=0
    g3: LineSegment StartX=-22.625 StartY=16.75 StartZ=0 EndX=-22.625 EndY=37.25 EndZ=0
    g4: GeomPoint X=7.125 Y=27 Z=0
    g5: Circle CenterX=-22.625 CenterY=27 CenterZ=0 NormalX=0 NormalY=0 NormalZ=1 AngleXU=0 Radius=1.25
    g6: Circle CenterX=7.125 CenterY=37.25 CenterZ=0 NormalX=0 NormalY=0 NormalZ=1 AngleXU=0 Radius=1.25
    g7: Circle CenterX=7.125 CenterY=16.75 CenterZ=0 NormalX=0 NormalY=0 NormalZ=1 AngleXU=0 Radius=1.25
    g8: LineSegment StartX=-7.125 StartY=37.25 StartZ=0 EndX=22.625 EndY=37.25 EndZ=0
    g9: LineSegment StartX=22.625 StartY=37.25 StartZ=0 EndX=22.625 EndY=16.75 EndZ=0
    g10: LineSegment StartX=22.625 StartY=16.75 StartZ=0 EndX=-7.125 EndY=16.75 EndZ=0
    g11: LineSegment StartX=-7.125 StartY=16.75 StartZ=0 EndX=-7.125 EndY=37.25 EndZ=0
    g12: Circle CenterX=-7.125 CenterY=37.25 CenterZ=0 NormalX=0 NormalY=0 NormalZ=1 AngleXU=0 Radius=1.25
    g13: Circle CenterX=-7.125 CenterY=16.75 CenterZ=0 NormalX=0 NormalY=0 NormalZ=1 AngleXU=0 Radius=1.25
    g14: Circle CenterX=22.625 CenterY=27 CenterZ=0 NormalX=0 NormalY=0 NormalZ=1 AngleXU=0 Radius=1.25
  constraints (37):
    c: Coincident(g0,g1)
    c: Coincident(g1,g2)
    c: Coincident(g2,g3)
    c: Coincident(g3,g0)
    c: Horizontal(g0)
    c: Horizontal(g2)
    c: Vertical(g1)
    c: Vertical(g3)
    c: DistanceY(g1,g0) = 20.5
    c: DistanceX(g-1,g1) = 7.125
    c: Symmetric(g1,g0,g4)
    c: Coincident(g6,g0)
    c: Coincident(g7,g1)
    c: Equal(g6,g5)
    c: Equal(g5,g7)
    c: Symmetric(g2,g0,g5)
    c: DistanceY(g-1,g4) = 27
    c: Diameter(g7) = 2.5
    c: DistanceX(g5,g-1) = 22.625
    c: Coincident(g8,g9)
    c: Coincident(g9,g10)
    c: Coincident(g10,g11)
    c: Coincident(g11,g8)
    c: Horizontal(g8)
    c: Horizontal(g10)
    c: Vertical(g9)
    c: Vertical(g11)
    c: PointOnObject(g8,g0)
    c: PointOnObject(g10,g2)
    c: Equal(g8,g0)
    c: DistanceX(g10,g-1) = 7.125
    c: Coincident(g12,g8)
    c: Coincident(g13,g10)
    c: Symmetric(g8,g9,g14)
    c: Equal(g6,g12)
    c: Equal(g13,g7)
    c: Equal(g7,g14)
FEATURE [PartDesign::Pocket] Pocket038  label="Pocket_USMtHoles"
  BaseFeature = -> Pad018
  Length = 5
  Length2 = 100
  Midplane = true
  Placement = pos=(0,0,0) rot=(1,0,0;1.5708rad)
  Profile = -> Sketch069
  Type = 1
FEATURE [PartDesign::Body] Body028  label="USShieldPlate"
  Group = -> [Sketch068,Pad018,Sketch069,Pocket038]
  Origin = -> Origin033
  Tip = -> Pocket038
FEATURE [PartDesign::Plane] DatumPlane007  label="Datum_BackPlate"
  AttachmentOffset = pos=(0,0,-4.8) rot=(0,0,1;0rad)
  Length = 61.4891
  MapMode = 5
  Placement = pos=(0,4.8,1.1e-15) rot=(1,0,0;1.5708rad)
  ResizeMode = 0
  Support = -> [XZ_Plane034]
  Width = 77.4891
  expr: .AttachmentOffset.Base.z = <<params>>.usr_mt_vert_thick_top * -1
FEATURE [Sketcher::SketchObject] Sketch070  label="Sketch_MainPlate"
  FullyConstrained = true
  MapMode = 5
  Placement = pos=(0,4.8,1.1e-15) rot=(1,0,0;1.5708rad)
  Support = -> [DatumPlane007]
  expr: Constraints[18] = <<shield_params>>.exp_leng
  expr: Constraints[19] = <<shield_params>>.exp_width
  expr: Constraints[20] = <<params>>.exp_i2c_mt_height
  sketch-geometry (9):
    g0: LineSegment StartX=-15 StartY=41 StartZ=0 EndX=15 EndY=41 EndZ=0
    g1: LineSegment StartX=16 StartY=40 StartZ=0 EndX=16 EndY=22 EndZ=0
    g2: LineSegment StartX=15 StartY=21 StartZ=0 EndX=-15 EndY=21 EndZ=0
    g3: LineSegment StartX=-16 StartY=22 StartZ=0 EndX=-16 EndY=40 EndZ=0
    g4: ArcOfCircle CenterX=-15 CenterY=40 CenterZ=0 NormalX=0 NormalY=0 NormalZ=1 AngleXU=0 Radius=1 StartAngle=1.5708 EndAngle=3.14159
    g5: ArcOfCircle CenterX=15 CenterY=40 CenterZ=0 NormalX=0 NormalY=0 NormalZ=1 AngleXU=0 Radius=1 StartAngle=6e-16 EndAngle=1.5708
    g6: ArcOfCircle CenterX=15 CenterY=22 CenterZ=0 NormalX=0 NormalY=0 NormalZ=1 AngleXU=0 Radius=1 StartAngle=4.71239 EndAngle=6.28319
    g7: ArcOfCircle CenterX=-15 CenterY=22 CenterZ=0 NormalX=0 NormalY=0 NormalZ=1 AngleXU=0 Radius=1 StartAngle=3.14159 EndAngle=4.71239
    g8: GeomPoint X=0 Y=31 Z=0
  constraints (21):
    c: Horizontal(g0)
    c: Horizontal(g2)
    c: Vertical(g1)
    c: Vertical(g3)
    c: Tangent(g3,g4) = 1.5708
    c: Tangent(g0,g4) = 1.5708
    c: Tangent(g0,g5) = 1.5708
    c: Tangent(g1,g5) = 1.5708
    c: Tangent(g1,g6) = 1.5708
    c: Tangent(g2,g6) = 1.5708
    c: Tangent(g2,g7) = 1.5708
    c: Tangent(g3,g7) = 1.5708
    c: PointOnObject(g8,g-2)
    c: Equal(g4,g5)
    c: Equal(g5,g6)
    c: Equal(g6,g7)
    c: Radius(g5) = 1
    c: Symmetric(g7,g5,g8)
    c: DistanceX(g3,g1) = 32
    c: DistanceY(g2,g0) = 20
    c: DistanceY(g-1,g8) = 31
FEATURE [PartDesign::Pad] Pad019  label="Pad_MainPlate001"
  Direction = (1,1,1)
  Length = 1.6
  Length2 = 100
  Placement = pos=(0,4.8,1e-15) rot=(1,0,0;1.5708rad)
  Profile = -> Sketch070
  Reversed = true
  Type = 0
  expr: Length = <<shield_params>>.exp_thick
FEATURE [Sketcher::SketchObject] Sketch071  label="Sketch_I2CExpMtHoles001"
  FullyConstrained = true
  MapMode = 5
  Placement = pos=(0,0,0) rot=(1,0,0;1.5708rad)
  Support = -> [XZ_Plane034]
  expr: Constraints[7] = <<params>>.m2_hole_clear_diam
  expr: Constraints[6] = <<params>>.exp_i2c_mt_height
  expr: Constraints[5] = <<params>>.exp_i2c_hole_space
  sketch-geometry (4):
    g0: Circle CenterX=-12.7 CenterY=31 CenterZ=0 NormalX=0 NormalY=0 NormalZ=1 AngleXU=0 Radius=1.25
    g1: Circle CenterX=12.7 CenterY=31 CenterZ=0 NormalX=0 NormalY=0 NormalZ=1 AngleXU=0 Radius=1.25
    g2: LineSegment StartX=-12.7 StartY=31 StartZ=0 EndX=12.7 EndY=31 EndZ=0
    g3: GeomPoint X=0 Y=31 Z=0
  constraints (9):
    c: Coincident(g2,g0)
    c: Coincident(g2,g1)
    c: Horizontal(g2)
    c: PointOnObject(g3,g-2)
    c: Symmetric(g0,g1,g3)
    c: DistanceX(g0,g1) = 25.4
    c: DistanceY(g-1,g3) = 31
    c: Diameter(g1) = 2.5
    c: Equal(g1,g0)
FEATURE [PartDesign::Pocket] Pocket039
  BaseFeature = -> Pad019
  Length = 5
  Length2 = 100
  Placement = pos=(0,4.8,1e-15) rot=(1,0,0;1.5708rad)
  Profile = -> Sketch071
  Type = 1
FEATURE [PartDesign::Body] Body029  label="I2CExpShieldPlate"
  Group = -> [DatumPlane007,Sketch070,Pad019,Sketch071,Pocket039]
  Origin = -> Origin034
  Tip = -> Pocket039
FEATURE [App::Part] Part  label="PB3D_USMount_Part"
  Group = -> [Body,Body028,Body029]
  Origin = -> Origin
FEATURE [Mesh::Feature] Mesh  label="I2CExpShieldPlate (Meshed)"
FEATURE [Mesh::Feature] Mesh001  label="USShieldPlate (Meshed)"
